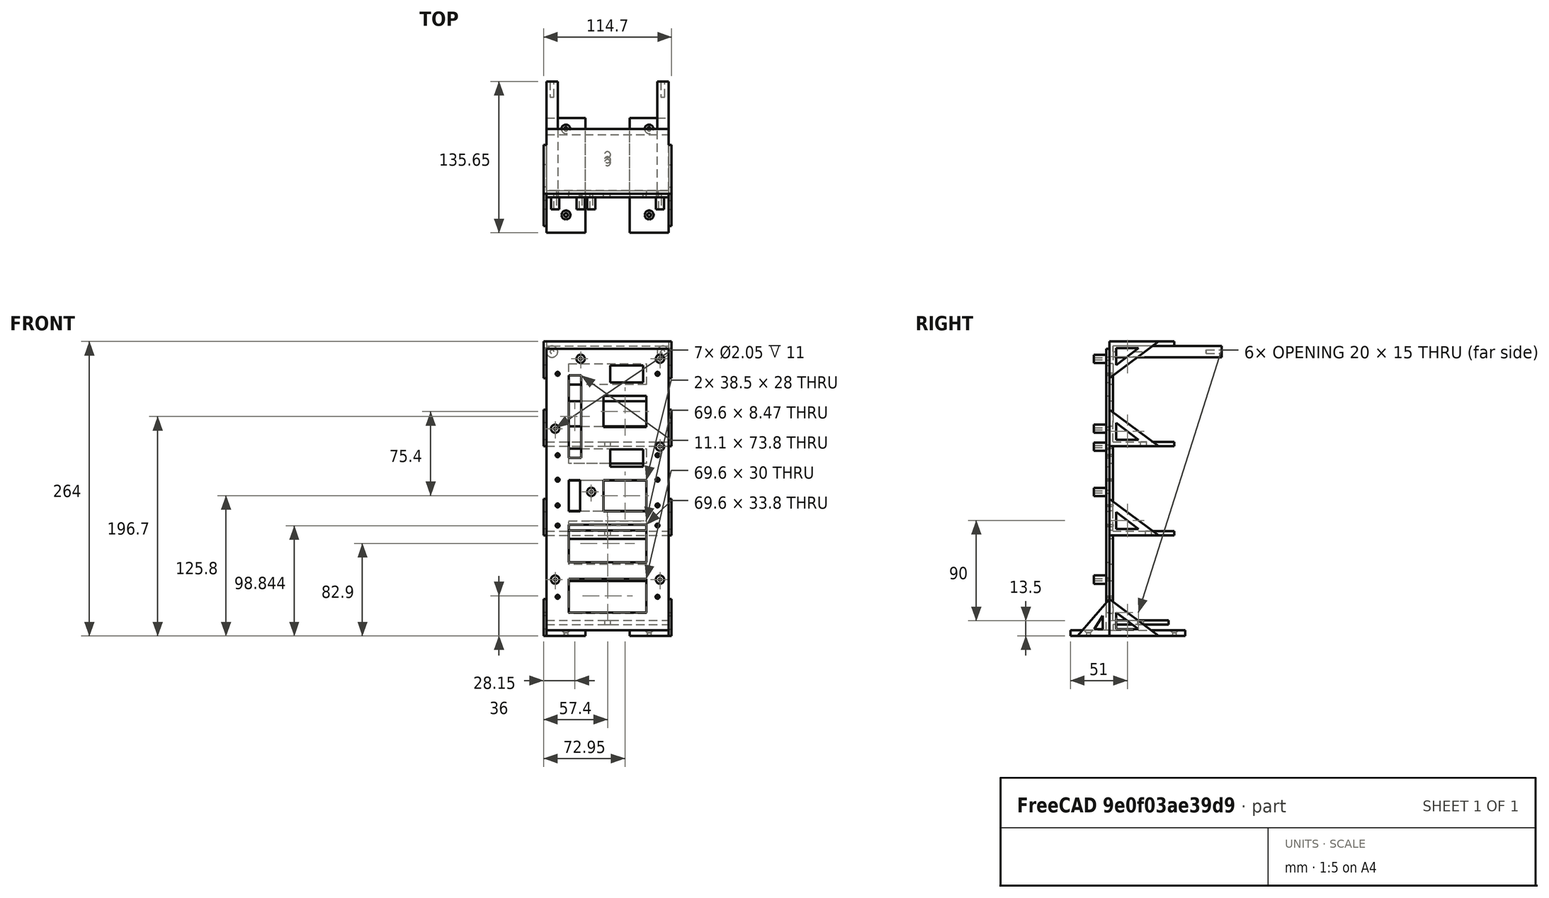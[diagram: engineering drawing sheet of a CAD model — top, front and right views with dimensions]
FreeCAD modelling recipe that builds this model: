
FCSTD DOCUMENT  (FreeCAD 1.0R39109 (Git))
Label: Tower
License: All rights reserved
LicenseURL: http://en.wikipedia.org/wiki/All_rights_reserved
objects: Sketcher::SketchObject×17, PartDesign::Pad×9, PartDesign::Plane×9, PartDesign::Pocket×4, PartDesign::Hole×3, PartDesign::Mirrored×2, PartDesign::Body×2, App::Link×1, App::Part×1
note: 97 computed .brp shape members not serialized (recipe doc carries the construction recipe); baked Part::Feature solids carry a one-line shape summary decoded from their .brp
EXTERNAL_REF file=../Master Document.FCStd obj=Spreadsheet

FEATURE [App::Link] Link  label="Monitor Chassis Parameters"
  LinkedObject = -> <external ../Master Document.FCStd>#Spreadsheet
FEATURE [Sketcher::SketchObject] Sketch  label="Backplate Sketch"
  ArcFitTolerance = 1e-06
  AttachmentSupport = -> [XZ_Plane001]
  FullyConstrained = true
  MakeInternals = false
  MapMode = 5
  Placement = pos=(0,0,0) rot=(1,0,0;1.5708rad)
  expr: Constraints[107] = <<Monitor Chassis Parameters>>.GSBackPlateMinimumSpanWidth
  expr: Constraints[108] = <<Monitor Chassis Parameters>>.GSBackPlateMinimumSpanWidth - 8
  expr: Constraints[109] = <<Monitor Chassis Parameters>>.GSBackPlateMinimumSpanWidth - 5
  expr: Constraints[10] = <<Monitor Chassis Parameters>>.GSComputeBoardWidth / 2 - <<Monitor Chassis Parameters>>.GSBackPlateTopInnerHoleInsetFromSide
  expr: Constraints[118] = 30
  expr: Constraints[119] = <<Monitor Chassis Parameters>>.GSBackPlateMiddleRightHoleHeight
  expr: Constraints[11] = <<Monitor Chassis Parameters>>.GSBackPlateBoltDiameter
  expr: Constraints[120] = <<Monitor Chassis Parameters>>.GSBackPlateTopHolesHeight
  expr: Constraints[122] = <<Monitor Chassis Parameters>>.GSBackPlateMiddleHoleHeight
  expr: Constraints[123] = <<Monitor Chassis Parameters>>.GSBackPlateBottomHoleHeight
  expr: Constraints[126] = <<Monitor Chassis Parameters>>.GSBackPlateLengthIncrement
  expr: Constraints[12] = <<Monitor Chassis Parameters>>.GSComputeBoardWidth / 2 - <<Monitor Chassis Parameters>>.GSBackPlateOuterHolesInsetFromSide
  expr: Constraints[130] = <<Monitor Chassis Parameters>>.GSBackPlateMinimumSpanWidth
  expr: Constraints[131] = <<Monitor Chassis Parameters>>.GSBackPlateMinimumSpanWidth + 4
  expr: Constraints[132] = <<Monitor Chassis Parameters>>.GSBackPlateMinimumSpanWidth
  expr: Constraints[133] = <<Monitor Chassis Parameters>>.GSBackPlateMinimumSpanWidth - 5
  expr: Constraints[134] = <<Monitor Chassis Parameters>>.GSBackPlateWidth
  expr: Constraints[135] = <<Monitor Chassis Parameters>>.GSBackPlateHeight
  expr: Constraints[136] = <<Monitor Chassis Parameters>>.GSBackPlateMiddleLeftHoleHeight
  expr: Constraints[138] = <<Monitor Chassis Parameters>>.GSBackPlateBoltDiameter
  expr: Constraints[13] = <<Monitor Chassis Parameters>>.GSBackPlateBoltDiameter
  expr: Constraints[14] = <<Monitor Chassis Parameters>>.GSComputeBoardWidth / 2 - <<Monitor Chassis Parameters>>.GSBackPlateOuterHolesInsetFromSide
  expr: Constraints[150] = <<Monitor Chassis Parameters>>.GSBackPlateVerticalOffset
  expr: Constraints[15] = <<Monitor Chassis Parameters>>.GSBackPlateBoltDiameter
  expr: Constraints[17] = <<Monitor Chassis Parameters>>.GSComputeBoardWidth / 2 - <<Monitor Chassis Parameters>>.GSBackPlateOuterHolesInsetFromSide
  expr: Constraints[18] = <<Monitor Chassis Parameters>>.GSBackPlateBoltDiameter
  expr: Constraints[19] = <<Monitor Chassis Parameters>>.GSBackPlateWidth / 2 - <<Monitor Chassis Parameters>>.GSBackPlateMiddleHoleOffsetFromLeftSide
  expr: Constraints[20] = <<Monitor Chassis Parameters>>.GSBackPlateBoltDiameter
  expr: Constraints[21] = <<Monitor Chassis Parameters>>.GSBackPlateBoltDiameter
  expr: Constraints[25] = <<Monitor Chassis Parameters>>.GSBackPlateWidthIncrement
  expr: Constraints[73] = <<Monitor Chassis Parameters>>.GSBackPlateMinimumSpanWidth
  expr: Constraints[7] = <<Monitor Chassis Parameters>>.GSComputeBoardHeight
  expr: Constraints[82] = <<Monitor Chassis Parameters>>.GSBackPlateMinimumSpanWidth
  expr: Constraints[8] = <<Monitor Chassis Parameters>>.GSComputeBoardWidth
  expr: Constraints[9] = <<Monitor Chassis Parameters>>.GSComputeBoardWidth / 2
  sketch-geometry (51):
    g0: LineSegment [constr] StartX=-50.8 StartY=20 StartZ=0 EndX=50.8 EndY=20 EndZ=0
    g1: LineSegment [constr] StartX=50.8 StartY=20 StartZ=0 EndX=50.8 EndY=248.6 EndZ=0
    g2: LineSegment [constr] StartX=50.8 StartY=248.6 StartZ=0 EndX=-50.8 EndY=248.6 EndZ=0
    g3: LineSegment [constr] StartX=-50.8 StartY=248.6 StartZ=0 EndX=-50.8 EndY=20 EndZ=0
    g4: Circle CenterX=-24.13 CenterY=243.52 CenterZ=0 NormalX=0 NormalY=0 NormalZ=1 AngleXU=0 Radius=1.4
    g5: Circle CenterX=46.99 CenterY=243.52 CenterZ=0 NormalX=0 NormalY=0 NormalZ=1 AngleXU=0 Radius=1.4
    g6: Circle CenterX=-46.99 CenterY=45.5 CenterZ=0 NormalX=0 NormalY=0 NormalZ=1 AngleXU=0 Radius=1.4
    g7: Circle CenterX=46.99 CenterY=45.5 CenterZ=0 NormalX=0 NormalY=0 NormalZ=1 AngleXU=0 Radius=1.4
    g8: Circle CenterX=-14.668 CenterY=124.14 CenterZ=0 NormalX=0 NormalY=0 NormalZ=1 AngleXU=0 Radius=1.4
    g9: Circle CenterX=-46.99 CenterY=180.78 CenterZ=0 NormalX=0 NormalY=0 NormalZ=1 AngleXU=0 Radius=1.4
    g10: Circle CenterX=46.99 CenterY=164.78 CenterZ=0 NormalX=0 NormalY=0 NormalZ=1 AngleXU=0 Radius=1.4
    g11: LineSegment StartX=-54.8 StartY=252.6 StartZ=0 EndX=-54.8 EndY=16 EndZ=0
    g12: LineSegment [constr] StartX=-54.8 StartY=16 StartZ=0 EndX=54.8 EndY=16 EndZ=0
    g13: LineSegment StartX=31.8 StartY=162.2 StartZ=0 EndX=2.4 EndY=162.2 EndZ=0
    g14: LineSegment StartX=2.4 StartY=162.2 StartZ=0 EndX=2.4 EndY=146.8 EndZ=0
    g15: LineSegment StartX=2.4 StartY=146.8 StartZ=0 EndX=31.8 EndY=146.8 EndZ=0
    g16: LineSegment StartX=31.8 StartY=146.8 StartZ=0 EndX=31.8 EndY=162.2 EndZ=0
    g17: LineSegment StartX=34.8 StartY=106.8 StartZ=0 EndX=-3.7 EndY=106.8 EndZ=0
    g18: LineSegment StartX=-3.7 StartY=106.8 StartZ=0 EndX=-3.7 EndY=134.8 EndZ=0
    g19: LineSegment StartX=-3.7 StartY=134.8 StartZ=0 EndX=34.8 EndY=134.8 EndZ=0
    g20: LineSegment StartX=34.8 StartY=134.8 StartZ=0 EndX=34.8 EndY=106.8 EndZ=0
    g21: LineSegment StartX=31.8 StartY=237.6 StartZ=0 EndX=2.4 EndY=237.6 EndZ=0
    g22: LineSegment StartX=2.4 StartY=237.6 StartZ=0 EndX=2.4 EndY=222.2 EndZ=0
    g23: LineSegment StartX=2.4 StartY=222.2 StartZ=0 EndX=31.8 EndY=222.2 EndZ=0
    g24: LineSegment StartX=31.8 StartY=222.2 StartZ=0 EndX=31.8 EndY=237.6 EndZ=0
    g25: LineSegment StartX=34.8 StartY=182.2 StartZ=0 EndX=-3.7 EndY=182.2 EndZ=0
    g26: LineSegment StartX=-3.7 StartY=182.2 StartZ=0 EndX=-3.7 EndY=210.2 EndZ=0
    g27: LineSegment StartX=-3.7 StartY=210.2 StartZ=0 EndX=34.8 EndY=210.2 EndZ=0
    g28: LineSegment StartX=34.8 StartY=210.2 StartZ=0 EndX=34.8 EndY=182.2 EndZ=0
    g29: LineSegment StartX=-34.8 StartY=228.6 StartZ=0 EndX=-34.8 EndY=154.8 EndZ=0
    g30: LineSegment StartX=-34.8 StartY=154.8 StartZ=0 EndX=-23.7 EndY=154.8 EndZ=0
    g31: LineSegment StartX=-23.7 StartY=154.8 StartZ=0 EndX=-23.7 EndY=228.6 EndZ=0
    g32: LineSegment StartX=-23.7 StartY=228.6 StartZ=0 EndX=-34.8 EndY=228.6 EndZ=0
    g33: LineSegment StartX=-34.8 StartY=134.8 StartZ=0 EndX=-34.8 EndY=106.8 EndZ=0
    g34: LineSegment StartX=-34.8 StartY=106.8 StartZ=0 EndX=-24.668 EndY=106.8 EndZ=0
    g35: LineSegment StartX=-24.668 StartY=106.8 StartZ=0 EndX=-24.668 EndY=134.8 EndZ=0
    g36: LineSegment StartX=-24.668 StartY=134.8 StartZ=0 EndX=-34.8 EndY=134.8 EndZ=0
    g37: LineSegment StartX=-34.8 StartY=94.8 StartZ=0 EndX=-34.8 EndY=61 EndZ=0
    g38: LineSegment StartX=-34.8 StartY=61 StartZ=0 EndX=34.8 EndY=61 EndZ=0
    g39: LineSegment StartX=34.8 StartY=61 StartZ=0 EndX=34.8 EndY=94.8 EndZ=0
    g40: LineSegment StartX=34.8 StartY=94.8 StartZ=0 EndX=-34.8 EndY=94.8 EndZ=0
    g41: LineSegment StartX=-34.8 StartY=46 StartZ=0 EndX=-34.8 EndY=16 EndZ=0
    g42: LineSegment StartX=-34.8 StartY=16 StartZ=0 EndX=34.8 EndY=16 EndZ=0
    g43: LineSegment StartX=34.8 StartY=16 StartZ=0 EndX=34.8 EndY=46 EndZ=0
    g44: LineSegment StartX=34.8 StartY=46 StartZ=0 EndX=-34.8 EndY=46 EndZ=0
    g45: LineSegment StartX=54.8 StartY=16 StartZ=0 EndX=54.8 EndY=252.6 EndZ=0
    g46: LineSegment StartX=-54.8 StartY=252.6 StartZ=0 EndX=54.8 EndY=252.6 EndZ=0
    g47: LineSegment StartX=-54.8 StartY=16 StartZ=0 EndX=-54.8 EndY=0 EndZ=0
    g48: LineSegment StartX=-54.8 StartY=0 StartZ=0 EndX=54.8 EndY=0 EndZ=0
    g49: LineSegment StartX=54.8 StartY=0 StartZ=0 EndX=54.8 EndY=16 EndZ=0
    g50: LineSegment [constr] StartX=54.8 StartY=16 StartZ=0 EndX=-54.8 EndY=16 EndZ=0
  constraints (152):
    c: Coincident(g0,g1)
    c: Coincident(g1,g2)
    c: Coincident(g2,g3)
    c: Coincident(g3,g0)
    c: Horizontal(g2)
    c: Vertical(g1)
    c: Vertical(g3)
    c: DistanceY(g0,g2) = 228.6
    c: DistanceX(g0,g0) = 101.6
    c: DistanceX(g0,g-1) = 50.8
    c: DistanceX(g4,g-1) = 24.13
    c: Diameter(g4) = 2.8
    c: DistanceX(g-1,g5) = 46.99
    c: Diameter(g6) = 2.8
    c: DistanceX(g6,g-1) = 46.99
    c: Diameter(g7) = 2.8
    c: Horizontal(g7,g6)
    c: DistanceX(g-1,g7) = 46.99
    c: Diameter(g8) = 2.8
    c: DistanceX(g8,g-1) = 14.668
    c: Diameter(g9) = 2.8
    c: Diameter(g10) = 2.8
    c: Coincident(g11,g12)
    c: Vertical(g11)
    c: Horizontal(g12)
    c: DistanceX(g11,g0) = 4
    c: Horizontal(g0)
    c: Vertical(g6,g9)
    c: Coincident(g13,g14)
    c: Coincident(g14,g15)
    c: Coincident(g15,g16)
    c: Coincident(g16,g13)
    c: Horizontal(g13)
    c: Horizontal(g15)
    c: Vertical(g14)
    c: Vertical(g16)
    c: Coincident(g17,g18)
    c: Coincident(g18,g19)
    c: Coincident(g19,g20)
    c: Coincident(g20,g17)
    c: Horizontal(g17)
    c: Horizontal(g19)
    c: Vertical(g18)
    c: Vertical(g20)
    c: DistanceX(g13,g13) = 29.4
    c: DistanceY(g14,g13) = 15.4
    c: DistanceX(g18,g19) = 38.5
    c: DistanceY(g17,g18) = 28
    c: DistanceY(g19,g15) = 12
    c: DistanceX(g15,g19) = 3
    c: Coincident(g21,g22)
    c: Coincident(g22,g23)
    c: Coincident(g23,g24)
    c: Coincident(g24,g21)
    c: Horizontal(g21)
    c: Horizontal(g23)
    c: Vertical(g22)
    c: Vertical(g24)
    c: Coincident(g25,g26)
    c: Coincident(g26,g27)
    c: Coincident(g27,g28)
    c: Coincident(g28,g25)
    c: Horizontal(g25)
    c: Horizontal(g27)
    c: Vertical(g26)
    c: Vertical(g28)
    c: DistanceX(g21,g21) = 29.4
    c: DistanceY(g22,g21) = 15.4
    c: DistanceX(g26,g27) = 38.5
    c: DistanceY(g25,g26) = 28
    c: DistanceY(g27,g23) = 12
    c: DistanceX(g23,g27) = 3
    c: Vertical(g19,g25)
    c: DistanceY(g13,g25) = 20
    c: Coincident(g29,g30)
    c: Coincident(g30,g31)
    c: Coincident(g31,g32)
    c: Coincident(g32,g29)
    c: Vertical(g29)
    c: Vertical(g31)
    c: Horizontal(g30)
    c: Horizontal(g32)
    c: DistanceX(g31,g26) = 20
    c: Coincident(g33,g34)
    c: Coincident(g34,g35)
    c: Coincident(g35,g36)
    c: Coincident(g36,g33)
    c: Vertical(g33)
    c: Vertical(g35)
    c: Horizontal(g34)
    c: Horizontal(g36)
    c: Coincident(g37,g38)
    c: Coincident(g38,g39)
    c: Coincident(g39,g40)
    c: Coincident(g40,g37)
    c: Vertical(g37)
    c: Vertical(g39)
    c: Horizontal(g38)
    c: Horizontal(g40)
    c: Coincident(g41,g42)
    c: Coincident(g42,g43)
    c: Coincident(g43,g44)
    c: Coincident(g44,g41)
    c: Vertical(g41)
    c: Vertical(g43)
    c: Horizontal(g42)
    c: Horizontal(g44)
    c: DistanceY(g33,g29) = 20
    c: DistanceY(g37,g33) = 12
    c: DistanceY(g41,g37) = 15
    c: Vertical(g29,g33)
    c: Vertical(g33,g37)
    c: Vertical(g37,g41)
    c: Vertical(g17,g39)
    c: Vertical(g39,g43)
    c: Horizontal(g35,g18)
    c: DistanceX(g35,g8) = 10
    c: Horizontal(g34,g17)
    c: DistanceY(g41,g41) = 30
    c: DistanceY(g0,g10) = 144.78
    c: DistanceY(g0,g4) = 223.52
    c: Horizontal(g5,g4)
    c: DistanceY(g0,g8) = 104.14
    c: DistanceY(g0,g6) = 25.5
    c: Coincident(g45,g12)
    c: Vertical(g45)
    c: DistanceY(g1,g45) = 4
    c: Horizontal(g11,g45)
    c: Coincident(g46,g11)
    c: Coincident(g46,g45)
    c: DistanceX(g11,g29) = 20
    c: DistanceY(g29,g11) = 24
    c: DistanceX(g27,g45) = 20
    c: DistanceY(g21,g45) = 15
    c: DistanceX(g11,g12) = 109.6
    c: DistanceY(g11,g11) = 236.6
    c: DistanceY(g0,g9) = 160.78
    c: Vertical(g7,g10)
    c: Diameter(g5) = 2.8
    c: Coincident(g47,g48)
    c: Coincident(g48,g49)
    c: Coincident(g49,g50)
    c: Coincident(g50,g47)
    c: Vertical(g47)
    c: Vertical(g49)
    c: Horizontal(g48)
    c: Horizontal(g50)
    c: Coincident(g47,g11)
    c: Horizontal(g48,g-1)
    c: Vertical(g49,g12)
    c: DistanceY(g-1,g0) = 20
    c: Horizontal(g41,g11)
FEATURE [PartDesign::Pad] Pad  label="Backplate Pad"
  Direction = (0,-1,2e-16)
  Length = 3
  Length2 = 10
  Placement = pos=(0,0,0) rot=(1,0,0;1.5708rad)
  Profile = -> Sketch
  ReferenceAxis = -> Sketch [N_Axis]
  Reversed = true
  Suppressed = false
  Type = 0
  expr: Length = <<Monitor Chassis Parameters>>.GSBackPlateThickness
FEATURE [Sketcher::SketchObject] Sketch001  label="Backplate Risers Sketch"
  ArcFitTolerance = 1e-06
  AttachmentSupport = -> [XZ_Plane001]
  FullyConstrained = true
  MakeInternals = false
  MapMode = 5
  Placement = pos=(0,0,0) rot=(1,0,0;1.5708rad)
  expr: Constraints[10] = <<Monitor Chassis Parameters>>.GSM2_5TappingScrewHoleDiameter
  expr: Constraints[11] = <<Monitor Chassis Parameters>>.GSM2_5TappingScrewHoleDiameter
  expr: Constraints[12] = <<Monitor Chassis Parameters>>.GSComputeBoardWidth / 2 - <<Monitor Chassis Parameters>>.GSBackPlateOuterHolesInsetFromSide
  expr: Constraints[13] = <<Monitor Chassis Parameters>>.GSM2_5TappingScrewHoleDiameter
  expr: Constraints[14] = <<Monitor Chassis Parameters>>.GSComputeBoardWidth / 2 - <<Monitor Chassis Parameters>>.GSBackPlateOuterHolesInsetFromSide
  expr: Constraints[15] = <<Monitor Chassis Parameters>>.GSM2_5TappingScrewHoleDiameter
  expr: Constraints[16] = <<Monitor Chassis Parameters>>.GSComputeBoardWidth / 2 - <<Monitor Chassis Parameters>>.GSBackPlateOuterHolesInsetFromSide
  expr: Constraints[17] = <<Monitor Chassis Parameters>>.GSM2_5TappingScrewHoleDiameter
  expr: Constraints[18] = <<Monitor Chassis Parameters>>.GSBackPlateWidth / 2 - <<Monitor Chassis Parameters>>.GSBackPlateMiddleHoleOffsetFromLeftSide
  expr: Constraints[19] = <<Monitor Chassis Parameters>>.GSM2_5TappingScrewHoleDiameter
  expr: Constraints[20] = <<Monitor Chassis Parameters>>.GSM2_5TappingScrewHoleDiameter
  expr: Constraints[25] = <<Monitor Chassis Parameters>>.GSBackPlateScrewHoleDiameter + 2 * <<Monitor Chassis Parameters>>.GSBackPlateStandoffWallThickness
  expr: Constraints[27] = <<Monitor Chassis Parameters>>.GSBackPlateScrewHoleDiameter + 2 * <<Monitor Chassis Parameters>>.GSBackPlateStandoffWallThickness
  expr: Constraints[33] = <<Monitor Chassis Parameters>>.GSBackPlateScrewHoleDiameter + 2 * <<Monitor Chassis Parameters>>.GSBackPlateStandoffWallThickness
  expr: Constraints[34] = <<Monitor Chassis Parameters>>.GSBackPlateScrewHoleDiameter + 2 * <<Monitor Chassis Parameters>>.GSBackPlateStandoffWallThickness
  expr: Constraints[35] = <<Monitor Chassis Parameters>>.GSBackPlateScrewHoleDiameter + 2 * <<Monitor Chassis Parameters>>.GSBackPlateStandoffWallThickness
  expr: Constraints[36] = <<Monitor Chassis Parameters>>.GSBackPlateScrewHoleDiameter + 2 * <<Monitor Chassis Parameters>>.GSBackPlateStandoffWallThickness
  expr: Constraints[37] = <<Monitor Chassis Parameters>>.GSBackPlateScrewHoleDiameter + 2 * <<Monitor Chassis Parameters>>.GSBackPlateStandoffWallThickness
  expr: Constraints[39] = <<Monitor Chassis Parameters>>.GSBackPlateMiddleLeftHoleHeight
  expr: Constraints[40] = <<Monitor Chassis Parameters>>.GSBackPlateBottomHoleHeight
  expr: Constraints[42] = <<Monitor Chassis Parameters>>.GSBackPlateMiddleHoleHeight
  expr: Constraints[43] = <<Monitor Chassis Parameters>>.GSBackPlateTopHolesHeight
  expr: Constraints[44] = <<Monitor Chassis Parameters>>.GSBackPlateMiddleRightHoleHeight
  expr: Constraints[45] = <<Monitor Chassis Parameters>>.GSBackPlateVerticalOffset
  expr: Constraints[6] = <<Monitor Chassis Parameters>>.GSComputeBoardHeight
  expr: Constraints[7] = <<Monitor Chassis Parameters>>.GSComputeBoardWidth
  expr: Constraints[8] = <<Monitor Chassis Parameters>>.GSComputeBoardWidth / 2
  expr: Constraints[9] = 0.5 * <<Monitor Chassis Parameters>>.GSComputeBoardWidth - <<Monitor Chassis Parameters>>.GSBackPlateTopInnerHoleInsetFromSide
  sketch-geometry (18):
    g0: LineSegment [constr] StartX=-50.8 StartY=20 StartZ=0 EndX=50.8 EndY=20 EndZ=0
    g1: LineSegment [constr] StartX=50.8 StartY=20 StartZ=0 EndX=50.8 EndY=248.6 EndZ=0
    g2: LineSegment [constr] StartX=50.8 StartY=248.6 StartZ=0 EndX=-50.8 EndY=248.6 EndZ=0
    g3: LineSegment [constr] StartX=-50.8 StartY=248.6 StartZ=0 EndX=-50.8 EndY=20 EndZ=0
    g4: Circle CenterX=-24.13 CenterY=243.52 CenterZ=0 NormalX=0 NormalY=0 NormalZ=1 AngleXU=0 Radius=1.025
    g5: Circle CenterX=46.99 CenterY=243.52 CenterZ=0 NormalX=0 NormalY=0 NormalZ=1 AngleXU=0 Radius=1.025
    g6: Circle CenterX=-46.99 CenterY=45.5 CenterZ=0 NormalX=0 NormalY=0 NormalZ=1 AngleXU=0 Radius=1.025
    g7: Circle CenterX=46.99 CenterY=45.5 CenterZ=0 NormalX=0 NormalY=0 NormalZ=1 AngleXU=0 Radius=1.025
    g8: Circle CenterX=-14.668 CenterY=124.14 CenterZ=0 NormalX=0 NormalY=0 NormalZ=1 AngleXU=0 Radius=1.025
    g9: Circle CenterX=-46.99 CenterY=180.78 CenterZ=0 NormalX=0 NormalY=0 NormalZ=1 AngleXU=0 Radius=1.025
    g10: Circle CenterX=46.99 CenterY=164.78 CenterZ=0 NormalX=0 NormalY=0 NormalZ=1 AngleXU=0 Radius=1.025
    g11: Circle CenterX=-24.13 CenterY=243.52 CenterZ=0 NormalX=0 NormalY=0 NormalZ=1 AngleXU=0 Radius=3.7
    g12: Circle CenterX=46.99 CenterY=243.52 CenterZ=0 NormalX=0 NormalY=0 NormalZ=1 AngleXU=0 Radius=3.7
    g13: Circle CenterX=-46.99 CenterY=180.78 CenterZ=0 NormalX=0 NormalY=0 NormalZ=1 AngleXU=0 Radius=3.7
    g14: Circle CenterX=46.99 CenterY=164.78 CenterZ=0 NormalX=0 NormalY=0 NormalZ=1 AngleXU=0 Radius=3.7
    g15: Circle CenterX=-14.668 CenterY=124.14 CenterZ=0 NormalX=0 NormalY=0 NormalZ=1 AngleXU=0 Radius=3.7
    g16: Circle CenterX=-46.99 CenterY=45.5 CenterZ=0 NormalX=0 NormalY=0 NormalZ=1 AngleXU=0 Radius=3.7
    g17: Circle CenterX=46.99 CenterY=45.5 CenterZ=0 NormalX=0 NormalY=0 NormalZ=1 AngleXU=0 Radius=3.7
  constraints (47):
    c: Coincident(g0,g1)
    c: Coincident(g1,g2)
    c: Coincident(g2,g3)
    c: Coincident(g3,g0)
    c: Vertical(g1)
    c: Vertical(g3)
    c: DistanceY(g0,g2) = 228.6
    c: DistanceX(g0,g0) = 101.6
    c: DistanceX(g0,g-1) = 50.8
    c: DistanceX(g4,g-1) = 24.13
    c: Diameter(g4) = 2.05
    c: Diameter(g5) = 2.05
    c: DistanceX(g-1,g5) = 46.99
    c: Diameter(g6) = 2.05
    c: DistanceX(g6,g-1) = 46.99
    c: Diameter(g7) = 2.05
    c: DistanceX(g-1,g7) = 46.99
    c: Diameter(g8) = 2.05
    c: DistanceX(g8,g-1) = 14.668
    c: Diameter(g9) = 2.05
    c: Diameter(g10) = 2.05
    c: Horizontal(g0)
    c: Vertical(g5,g10)
    c: Horizontal(g5,g4)
    c: Coincident(g11,g4)
    c: Diameter(g11) = 7.4
    c: Coincident(g12,g5)
    c: Diameter(g12) = 7.4
    c: Coincident(g13,g9)
    c: Coincident(g14,g10)
    c: Coincident(g15,g8)
    c: Coincident(g16,g6)
    c: Coincident(g17,g7)
    c: Diameter(g17) = 7.4
    c: Diameter(g16) = 7.4
    c: Diameter(g15) = 7.4
    c: Diameter(g14) = 7.4
    c: Diameter(g13) = 7.4
    c: Vertical(g9,g6)
    c: DistanceY(g0,g9) = 160.78
    c: DistanceY(g0,g6) = 25.5
    c: Horizontal(g7,g6)
    c: DistanceY(g0,g8) = 104.14
    c: DistanceY(g0,g4) = 223.52
    c: DistanceY(g0,g10) = 144.78
    c: DistanceY(g-1,g0) = 20
    c: Horizontal(g2,g1)
FEATURE [PartDesign::Pad] Pad001  label="Backplate Risers Pad"
  BaseFeature = -> Pad
  Direction = (0,-1,2e-16)
  Length = 11
  Length2 = 10
  Placement = pos=(0,0,0) rot=(1,0,0;1.5708rad)
  Profile = -> Sketch001
  ReferenceAxis = -> Sketch001 [N_Axis]
  Suppressed = false
  Type = 0
  expr: Length = <<Monitor Chassis Parameters>>.GSBackPlateStandoffHeight
FEATURE [Sketcher::SketchObject] Sketch002  label="Backplate Foot Sketch"
  ArcFitTolerance = 1e-06
  AttachmentSupport = -> [XZ_Plane001]
  FullyConstrained = true
  MakeInternals = false
  MapMode = 5
  Placement = pos=(0,0,0) rot=(1,0,0;1.5708rad)
  expr: Constraints[11] = <<Monitor Chassis Parameters>>.GSTowerFeetThickness
  expr: Constraints[21] = <<Monitor Chassis Parameters>>.GSTowerFeetThickness
  expr: Constraints[22] = <<Monitor Chassis Parameters>>.GSBackPlateFootWidth
  expr: Constraints[23] = 0.5 * <<Monitor Chassis Parameters>>.GSBackPlateWidth
  expr: Constraints[8] = <<Monitor Chassis Parameters>>.GSBackPlateFootWidth
  expr: Constraints[9] = 0.5 * <<Monitor Chassis Parameters>>.GSBackPlateWidth
  sketch-geometry (8):
    g0: LineSegment StartX=-54.8 StartY=-5 StartZ=0 EndX=-19.8 EndY=-5 EndZ=0
    g1: LineSegment StartX=-19.8 StartY=-5 StartZ=0 EndX=-19.8 EndY=0 EndZ=0
    g2: LineSegment StartX=-19.8 StartY=0 StartZ=0 EndX=-54.8 EndY=0 EndZ=0
    g3: LineSegment StartX=-54.8 StartY=0 StartZ=0 EndX=-54.8 EndY=-5 EndZ=0
    g4: LineSegment StartX=54.8 StartY=-5 StartZ=0 EndX=54.8 EndY=0 EndZ=0
    g5: LineSegment StartX=54.8 StartY=0 StartZ=0 EndX=19.8 EndY=0 EndZ=0
    g6: LineSegment StartX=19.8 StartY=0 StartZ=0 EndX=19.8 EndY=-5 EndZ=0
    g7: LineSegment StartX=19.8 StartY=-5 StartZ=0 EndX=54.8 EndY=-5 EndZ=0
  constraints (24):
    c: Coincident(g0,g1)
    c: Coincident(g1,g2)
    c: Coincident(g2,g3)
    c: Coincident(g3,g0)
    c: Horizontal(g0)
    c: Horizontal(g2)
    c: Vertical(g1)
    c: Vertical(g3)
    c: DistanceX(g2,g1) = 35
    c: DistanceX(g2,g-1) = 54.8
    c: Horizontal(g2,g-1)
    c: DistanceY(g0,g2) = 5
    c: Coincident(g4,g5)
    c: Coincident(g5,g6)
    c: Coincident(g6,g7)
    c: Coincident(g7,g4)
    c: Vertical(g4)
    c: Vertical(g6)
    c: Horizontal(g5)
    c: Horizontal(g7)
    c: Horizontal(g5,g-1)
    c: DistanceY(g4,g4) = 5
    c: DistanceX(g6,g4) = 35
    c: DistanceX(g-1,g4) = 54.8
FEATURE [PartDesign::Pad] Pad002  label="Backplate Foot Pad"
  BaseFeature = -> Pad001
  Direction = (0,-1,2e-16)
  Length = 32
  Length2 = 3
  Placement = pos=(0,0,0) rot=(1,0,0;1.5708rad)
  Profile = -> Sketch002
  ReferenceAxis = -> Sketch002 [N_Axis]
  Suppressed = false
  Type = 4
  expr: Length = <<Monitor Chassis Parameters>>.GSBackPlateFootLengthBackward
  expr: Length2 = <<Monitor Chassis Parameters>>.GSBackPlateThickness
FEATURE [Sketcher::SketchObject] Sketch003  label="Backplate Foot Screw Holes Sketch"
  ArcFitTolerance = 1e-06
  AttachmentSupport = -> [XY_Plane001]
  FullyConstrained = true
  MakeInternals = false
  MapMode = 5
  expr: Constraints[0] = 0.5 * <<Monitor Chassis Parameters>>.GSBackPlateFootLengthBackward
  expr: Constraints[1] = 0.5 * <<Monitor Chassis Parameters>>.GSBackPlateWidth - 0.5 * <<Monitor Chassis Parameters>>.GSBackPlateFootWidth
  expr: Constraints[2] = 0.5 * <<Monitor Chassis Parameters>>.GSBackPlateWidth - 0.5 * <<Monitor Chassis Parameters>>.GSBackPlateFootWidth
  expr: Constraints[3] = <<Monitor Chassis Parameters>>.GSTowerFeetScrewDiameter
  expr: Constraints[4] = <<Monitor Chassis Parameters>>.GSTowerFeetScrewDiameter
  sketch-geometry (2):
    g0: Circle CenterX=-37.3 CenterY=-16 CenterZ=0 NormalX=0 NormalY=0 NormalZ=1 AngleXU=0 Radius=1.7
    g1: Circle CenterX=37.3 CenterY=-16 CenterZ=0 NormalX=0 NormalY=0 NormalZ=1 AngleXU=0 Radius=1.7
  constraints (6):
    c: DistanceY(g0,g-1) = 16
    c: DistanceX(g0,g-1) = 37.3
    c: DistanceX(g-1,g1) = 37.3
    c: Diameter(g0) = 3.4
    c: Diameter(g1) = 3.4
    c: Horizontal(g1,g0)
FEATURE [PartDesign::Hole] Hole  label="Backplate Foot Screw Holes"
  BaseFeature = -> Pad002
  CustomThreadClearance = 0
  Depth = 25
  DepthType = 0
  Diameter = 3.4
  DrillForDepth = false
  DrillPoint = 1
  DrillPointAngle = 118
  HoleCutCountersinkAngle = 90
  HoleCutCustomValues = false
  HoleCutDepth = 0
  HoleCutDiameter = 8
  HoleCutType = 2
  ModelThread = false
  Placement = pos=(0,0,0) rot=(1,0,0;1.5708rad)
  Profile = -> Sketch003
  Suppressed = false
  Tapered = false
  TaperedAngle = 90
  ThreadClass = 0
  ThreadDepth = 25
  ThreadDepthType = 0
  ThreadDirection = 0
  ThreadFit = 0
  ThreadSize = 0
  ThreadType = 0
  Threaded = false
  UseCustomThreadClearance = false
  expr: Diameter = <<Monitor Chassis Parameters>>.GSTowerFeetScrewDiameter
  expr: HoleCutDiameter = <<Monitor Chassis Parameters>>.GSM4BoltCountersinkDiameter
FEATURE [PartDesign::Plane] DatumPlane
  AttachmentOffset = pos=(0,0,54.8) rot=(0,0,1;0rad)
  AttachmentSupport = -> [YZ_Plane001]
  Length = 82.1581
  MapMode = 5
  Placement = pos=(54.8,0,0) rot=(0.57735,0.57735,0.57735;2.0944rad)
  ResizeMode = 0
  Width = 302.758
  expr: .AttachmentOffset.Base.z = 0.5 * <<Monitor Chassis Parameters>>.GSBackPlateWidth
FEATURE [Sketcher::SketchObject] Sketch004  label="Foot Support Corner Sketch"
  ArcFitTolerance = 1e-06
  AttachmentSupport = -> [DatumPlane]
  FullyConstrained = true
  MakeInternals = false
  MapMode = 5
  Placement = pos=(54.8,0,0) rot=(0.57735,0.57735,0.57735;2.0944rad)
  expr: Constraints[14] = <<Monitor Chassis Parameters>>.GSSideCornerCutoutInset
  expr: Constraints[15] = <<Monitor Chassis Parameters>>.GSSideCornerCutoutInset
  expr: Constraints[16] = 2.5 * <<Monitor Chassis Parameters>>.GSSideCornerCutoutInset
  expr: Constraints[17] = 2.5 * <<Monitor Chassis Parameters>>.GSSideCornerCutoutInset
  expr: Constraints[1] = <<Monitor Chassis Parameters>>.GSBackPlateThickness
  expr: Constraints[4] = <<Monitor Chassis Parameters>>.GSTowerFeetThickness
  expr: Constraints[7] = 0.9 * <<Monitor Chassis Parameters>>.GSBackPlateFootLengthBackward
  expr: Constraints[8] = 0.6 * <<Monitor Chassis Parameters>>.GSTowerFloorDepth
  sketch-geometry (6):
    g0: LineSegment StartX=-25.8 StartY=-5 StartZ=0 EndX=3 EndY=-5 EndZ=0
    g1: LineSegment StartX=3 StartY=28 StartZ=0 EndX=3 EndY=-5 EndZ=0
    g2: LineSegment StartX=-25.8 StartY=-5 StartZ=0 EndX=3 EndY=28 EndZ=0
    g3: LineSegment StartX=-10.8 StartY=1 StartZ=0 EndX=-3 EndY=13 EndZ=0
    g4: LineSegment StartX=-3 StartY=13 StartZ=0 EndX=-3 EndY=1 EndZ=0
    g5: LineSegment StartX=-10.8 StartY=1 StartZ=0 EndX=-3 EndY=1 EndZ=0
  constraints (18):
    c: Horizontal(g0)
    c: DistanceX(g-1,g0) = 3
    c: Coincident(g1,g0)
    c: Vertical(g1)
    c: DistanceY(g0,g-1) = 5
    c: Coincident(g2,g0)
    c: Coincident(g2,g1)
    c: DistanceX(g0,g0) = 28.8
    c: DistanceY(g0,g1) = 33
    c: Coincident(g4,g3)
    c: Vertical(g4)
    c: Coincident(g5,g3)
    c: Coincident(g5,g4)
    c: Horizontal(g5)
    c: DistanceY(g0,g4) = 6
    c: DistanceX(g4,g0) = 6
    c: DistanceX(g0,g3) = 15
    c: DistanceY(g3,g1) = 15
FEATURE [PartDesign::Pad] Pad003  label="Foot Support Corner Pad"
  BaseFeature = -> Hole
  Direction = (1,0,0)
  Length = 2.5
  Length2 = 10
  Placement = pos=(0,0,0) rot=(1,0,0;1.5708rad)
  Profile = -> Sketch004
  ReferenceAxis = -> Sketch004 [N_Axis]
  Suppressed = false
  Type = 0
  expr: Length = <<Monitor Chassis Parameters>>.GSSideCornerThickness
FEATURE [PartDesign::Mirrored] Mirrored  label="Foot Support Corner Mirrored"
  BaseFeature = -> Pad003
  MirrorPlane = -> YZ_Plane001
  Originals = -> [Pad003]
  Placement = pos=(0,0,0) rot=(1,0,0;1.5708rad)
  Suppressed = false
  TransformMode = 0
FEATURE [PartDesign::Plane] DatumPlane001
  AttachmentOffset = pos=(0,0,54.8) rot=(0,0,1;0rad)
  AttachmentSupport = -> [YZ_Plane002]
  Length = 159.977
  MapMode = 5
  Placement = pos=(54.8,0,0) rot=(0.57735,0.57735,0.57735;2.0944rad)
  ResizeMode = 0
  Width = 321.327
  expr: .AttachmentOffset.Base.z = 0.5 * <<Monitor Chassis Parameters>>.GSBackPlateWidth
FEATURE [Sketcher::SketchObject] Sketch005  label="Frontplate Sketch"
  ArcFitTolerance = 1e-06
  AttachmentSupport = -> [XZ_Plane002]
  FullyConstrained = false
  MakeInternals = false
  MapMode = 5
  Placement = pos=(0,0,0) rot=(1,0,0;1.5708rad)
  expr: Constraints[105] = <<Monitor Chassis Parameters>>.GSFrontPlateMinimumSpanWidth - 5
  expr: Constraints[106] = <<Monitor Chassis Parameters>>.GSTowerFourthFloorHeight + <<Monitor Chassis Parameters>>.GSTowerFloorThickness
  expr: Constraints[107] = <<Monitor Chassis Parameters>>.GSTowerLayerJoinScrewDiameter
  expr: Constraints[108] = <<Monitor Chassis Parameters>>.GSTowerLayerJoinScrewDiameter
  expr: Constraints[110] = <<Monitor Chassis Parameters>>.GSTowerLayerJoinScrewInset
  expr: Constraints[111] = <<Monitor Chassis Parameters>>.GSTowerLayerJoinScrewInset
  expr: Constraints[112] = <<Monitor Chassis Parameters>>.GSTowerLayerJoinScrewDiameter
  expr: Constraints[113] = <<Monitor Chassis Parameters>>.GSTowerLayerJoinScrewDiameter
  expr: Constraints[115] = <<Monitor Chassis Parameters>>.GSTowerLayerJoinScrewDiameter
  expr: Constraints[116] = <<Monitor Chassis Parameters>>.GSTowerLayerJoinScrewDiameter
  expr: Constraints[120] = <<Monitor Chassis Parameters>>.GSTowerLayerJoinScrewDiameter
  expr: Constraints[121] = <<Monitor Chassis Parameters>>.GSTowerLayerJoinScrewDiameter
  expr: Constraints[123] = <<Monitor Chassis Parameters>>.GSTowerLayerJoinScrewHeightFromFoot_1
  expr: Constraints[124] = <<Monitor Chassis Parameters>>.GSTowerLayerJoinScrewHeightFromFoot_3
  expr: Constraints[126] = <<Monitor Chassis Parameters>>.GSTowerLayerJoinScrewHeightFromFoot_4
  expr: Constraints[127] = <<Monitor Chassis Parameters>>.GSTowerLayerJoinScrewHeightFromFoot_5
  expr: Constraints[129] = <<Monitor Chassis Parameters>>.GSTowerLayerJoinScrewDiameter
  expr: Constraints[130] = <<Monitor Chassis Parameters>>.GSTowerLayerJoinScrewDiameter
  expr: Constraints[133] = <<Monitor Chassis Parameters>>.GSTowerLayerJoinScrewHeightFromFoot_6
  expr: Constraints[13] = <<Monitor Chassis Parameters>>.GSBackPlateWidthIncrement
  expr: Constraints[145] = <<Monitor Chassis Parameters>>.GSTowerLayerJoinScrewDiameter
  expr: Constraints[150] = <<Monitor Chassis Parameters>>.GSTowerLayerJoinScrewHeightFromFoot_2
  expr: Constraints[46] = <<Monitor Chassis Parameters>>.GSFrontPlateMinimumSpanWidth - 5
  expr: Constraints[48] = <<Monitor Chassis Parameters>>.GSFrontPlateMinimumSpanWidth
  expr: Constraints[65] = <<Monitor Chassis Parameters>>.GSFrontPlateMinimumSpanWidth - 5
  expr: Constraints[71] = <<Monitor Chassis Parameters>>.GSBackPlateLengthIncrement
  expr: Constraints[75] = <<Monitor Chassis Parameters>>.GSBackPlateWidth
  expr: Constraints[76] = <<Monitor Chassis Parameters>>.GSBackPlateVerticalOffset
  expr: Constraints[7] = <<Monitor Chassis Parameters>>.GSComputeBoardHeight
  expr: Constraints[8] = <<Monitor Chassis Parameters>>.GSComputeBoardWidth
  expr: Constraints[96] = <<Monitor Chassis Parameters>>.GSFrontPlateMinimumSpanWidth - 5
  expr: Constraints[97] = <<Monitor Chassis Parameters>>.GSFrontPlateMinimumSpanWidth
  expr: Constraints[98] = <<Monitor Chassis Parameters>>.GSFrontPlateMinimumSpanWidth
  expr: Constraints[9] = <<Monitor Chassis Parameters>>.GSComputeBoardWidth / 2
  sketch-geometry (55):
    g0: LineSegment [constr] StartX=-50.8 StartY=24 StartZ=0 EndX=50.8 EndY=24 EndZ=0
    g1: LineSegment [constr] StartX=50.8 StartY=24 StartZ=0 EndX=50.8 EndY=252.6 EndZ=0
    g2: LineSegment [constr] StartX=50.8 StartY=252.6 StartZ=0 EndX=-50.8 EndY=252.6 EndZ=0
    g3: LineSegment [constr] StartX=-50.8 StartY=252.6 StartZ=0 EndX=-50.8 EndY=24 EndZ=0
    g4: LineSegment StartX=-54.8 StartY=256.6 StartZ=0 EndX=-54.8 EndY=20 EndZ=0
    g5: LineSegment [constr] StartX=-54.8 StartY=20 StartZ=0 EndX=54.8 EndY=20 EndZ=0
    g6: LineSegment StartX=34.8 StartY=162.959 StartZ=0 EndX=-34.8 EndY=162.959 EndZ=0
    g7: LineSegment StartX=-34.8 StartY=162.959 StartZ=0 EndX=-34.8 EndY=149.512 EndZ=0
    g8: LineSegment StartX=-34.8 StartY=149.512 StartZ=0 EndX=34.8 EndY=149.512 EndZ=0
    g9: LineSegment StartX=34.8 StartY=149.512 StartZ=0 EndX=34.8 EndY=162.959 EndZ=0
    g10: LineSegment StartX=34.8 StartY=107.062 StartZ=0 EndX=-34.8 EndY=107.062 EndZ=0
    g11: LineSegment StartX=-34.8 StartY=107.062 StartZ=0 EndX=-34.8 EndY=134.512 EndZ=0
    g12: LineSegment StartX=-34.8 StartY=134.512 StartZ=0 EndX=34.8 EndY=134.512 EndZ=0
    g13: LineSegment StartX=34.8 StartY=134.512 StartZ=0 EndX=34.8 EndY=107.062 EndZ=0
    g14: LineSegment StartX=34.8 StartY=239 StartZ=0 EndX=-34.8 EndY=239 EndZ=0
    g15: LineSegment StartX=-34.8 StartY=239 StartZ=0 EndX=-34.8 EndY=220.485 EndZ=0
    g16: LineSegment StartX=-34.8 StartY=220.485 StartZ=0 EndX=34.8 EndY=220.485 EndZ=0
    g17: LineSegment StartX=34.8 StartY=220.485 StartZ=0 EndX=34.8 EndY=239 EndZ=0
    g18: LineSegment StartX=34.8 StartY=182.959 StartZ=0 EndX=-34.8 EndY=182.959 EndZ=0
    g19: LineSegment StartX=-34.8 StartY=182.959 StartZ=0 EndX=-34.8 EndY=205.485 EndZ=0
    g20: LineSegment StartX=-34.8 StartY=205.485 StartZ=0 EndX=34.8 EndY=205.485 EndZ=0
    g21: LineSegment StartX=34.8 StartY=205.485 StartZ=0 EndX=34.8 EndY=182.959 EndZ=0
    g22: LineSegment StartX=-34.8 StartY=81.9803 StartZ=0 EndX=-34.8 EndY=59.2632 EndZ=0
    g23: LineSegment StartX=-34.8 StartY=59.2632 StartZ=0 EndX=34.8 EndY=59.2632 EndZ=0
    g24: LineSegment StartX=34.8 StartY=59.2632 StartZ=0 EndX=34.8 EndY=81.9803 EndZ=0
    g25: LineSegment StartX=34.8 StartY=81.9803 StartZ=0 EndX=-34.8 EndY=81.9803 EndZ=0
    g26: LineSegment StartX=-34.8 StartY=44.2632 StartZ=0 EndX=-34.8 EndY=15 EndZ=0
    g27: LineSegment StartX=-34.8 StartY=15 StartZ=0 EndX=34.8 EndY=15 EndZ=0
    g28: LineSegment StartX=34.8 StartY=15 StartZ=0 EndX=34.8 EndY=44.2632 EndZ=0
    g29: LineSegment StartX=34.8 StartY=44.2632 StartZ=0 EndX=-34.8 EndY=44.2632 EndZ=0
    g30: LineSegment StartX=54.8 StartY=20 StartZ=0 EndX=54.8 EndY=256.6 EndZ=0
    g31: LineSegment [constr] StartX=-54.8 StartY=256.6 StartZ=0 EndX=54.8 EndY=256.6 EndZ=0
    g32: LineSegment StartX=-54.8 StartY=20 StartZ=0 EndX=-54.8 EndY=0 EndZ=0
    g33: LineSegment StartX=-54.8 StartY=0 StartZ=0 EndX=54.8 EndY=0 EndZ=0
    g34: LineSegment StartX=54.8 StartY=0 StartZ=0 EndX=54.8 EndY=20 EndZ=0
    g35: LineSegment [constr] StartX=54.8 StartY=20 StartZ=0 EndX=-54.8 EndY=20 EndZ=0
    g36: LineSegment StartX=-54.8 StartY=256.6 StartZ=0 EndX=-54.8 EndY=259 EndZ=0
    g37: LineSegment StartX=-54.8 StartY=259 StartZ=0 EndX=54.8 EndY=259 EndZ=0
    g38: LineSegment StartX=54.8 StartY=259 StartZ=0 EndX=54.8 EndY=256.6 EndZ=0
    g39: Circle CenterX=-44.8 CenterY=30 CenterZ=0 NormalX=0 NormalY=0 NormalZ=1 AngleXU=0 Radius=0.855
    g40: Circle CenterX=44.8 CenterY=30 CenterZ=0 NormalX=0 NormalY=0 NormalZ=1 AngleXU=0 Radius=0.855
    g41: Circle CenterX=-44.8 CenterY=112 CenterZ=0 NormalX=0 NormalY=0 NormalZ=1 AngleXU=0 Radius=0.855
    g42: Circle CenterX=44.8 CenterY=112 CenterZ=0 NormalX=0 NormalY=0 NormalZ=1 AngleXU=0 Radius=0.855
    g43: Circle CenterX=-44.8 CenterY=157 CenterZ=0 NormalX=0 NormalY=0 NormalZ=1 AngleXU=0 Radius=0.855
    g44: Circle CenterX=44.8 CenterY=157 CenterZ=0 NormalX=0 NormalY=0 NormalZ=1 AngleXU=0 Radius=0.855
    g45: Circle CenterX=-44.8 CenterY=135 CenterZ=0 NormalX=0 NormalY=0 NormalZ=1 AngleXU=0 Radius=0.855
    g46: Circle CenterX=44.8 CenterY=135 CenterZ=0 NormalX=0 NormalY=0 NormalZ=1 AngleXU=0 Radius=0.855
    g47: Circle CenterX=-44.8 CenterY=230 CenterZ=0 NormalX=0 NormalY=0 NormalZ=1 AngleXU=0 Radius=0.855
    g48: Circle CenterX=44.8 CenterY=230 CenterZ=0 NormalX=0 NormalY=0 NormalZ=1 AngleXU=0 Radius=0.855
    g49: LineSegment StartX=-34.8 StartY=89.607 StartZ=0 EndX=34.8 EndY=89.607 EndZ=0
    g50: LineSegment StartX=34.8 StartY=89.607 StartZ=0 EndX=34.8 EndY=98.0817 EndZ=0
    g51: LineSegment StartX=34.8 StartY=98.0817 StartZ=0 EndX=-34.8 EndY=98.0817 EndZ=0
    g52: LineSegment StartX=-34.8 StartY=98.0817 StartZ=0 EndX=-34.8 EndY=89.607 EndZ=0
    g53: Circle CenterX=-44.8 CenterY=94 CenterZ=0 NormalX=0 NormalY=0 NormalZ=1 AngleXU=0 Radius=0.855
    g54: Circle CenterX=44.8 CenterY=94 CenterZ=0 NormalX=0 NormalY=0 NormalZ=1 AngleXU=0 Radius=0.85
  constraints (151):
    c: Coincident(g0,g1)
    c: Coincident(g1,g2)
    c: Coincident(g2,g3)
    c: Coincident(g3,g0)
    c: Horizontal(g2)
    c: Vertical(g1)
    c: Vertical(g3)
    c: DistanceY(g0,g2) = 228.6
    c: DistanceX(g0,g0) = 101.6
    c: DistanceX(g0,g-1) = 50.8
    c: Coincident(g4,g5)
    c: Vertical(g4)
    c: Horizontal(g5)
    c: DistanceX(g4,g0) = 4
    c: Horizontal(g0)
    c: Coincident(g6,g7)
    c: Coincident(g7,g8)
    c: Coincident(g8,g9)
    c: Coincident(g9,g6)
    c: Horizontal(g6)
    c: Horizontal(g8)
    c: Vertical(g7)
    c: Vertical(g9)
    c: Coincident(g10,g11)
    c: Coincident(g11,g12)
    c: Coincident(g12,g13)
    c: Coincident(g13,g10)
    c: Horizontal(g10)
    c: Horizontal(g12)
    c: Vertical(g11)
    c: Vertical(g13)
    c: Coincident(g14,g15)
    c: Coincident(g15,g16)
    c: Coincident(g16,g17)
    c: Coincident(g17,g14)
    c: Horizontal(g14)
    c: Horizontal(g16)
    c: Vertical(g15)
    c: Vertical(g17)
    c: Coincident(g18,g19)
    c: Coincident(g19,g20)
    c: Coincident(g20,g21)
    c: Coincident(g21,g18)
    c: Horizontal(g18)
    c: Horizontal(g20)
    c: Vertical(g19)
    c: DistanceY(g20,g16) = 15
    c: Vertical(g12,g18)
    c: DistanceY(g6,g18) = 20
    c: Coincident(g22,g23)
    c: Coincident(g23,g24)
    c: Coincident(g24,g25)
    c: Coincident(g25,g22)
    c: Vertical(g22)
    c: Vertical(g24)
    c: Horizontal(g23)
    c: Horizontal(g25)
    c: Coincident(g26,g27)
    c: Coincident(g27,g28)
    c: Coincident(g28,g29)
    c: Coincident(g29,g26)
    c: Vertical(g26)
    c: Vertical(g28)
    c: Horizontal(g27)
    c: Horizontal(g29)
    c: DistanceY(g26,g22) = 15
    c: Vertical(g22,g26)
    c: Vertical(g10,g24)
    c: Vertical(g24,g28)
    c: Coincident(g30,g5)
    c: Vertical(g30)
    c: DistanceY(g1,g30) = 4
    c: Horizontal(g4,g30)
    c: Coincident(g31,g4)
    c: Coincident(g31,g30)
    c: DistanceX(g4,g5) = 109.6
    c: DistanceY(g-1,g5) = 20
    c: Coincident(g32,g33)
    c: Coincident(g33,g34)
    c: Coincident(g34,g35)
    c: Coincident(g35,g32)
    c: Vertical(g32)
    c: Vertical(g34)
    c: Horizontal(g33)
    c: Horizontal(g35)
    c: Coincident(g32,g4)
    c: Horizontal(g33,g-1)
    c: Vertical(g34,g5)
    c: Vertical(g21)
    c: Coincident(g36,g4)
    c: Vertical(g36)
    c: Coincident(g37,g36)
    c: Horizontal(g37)
    c: Coincident(g38,g37)
    c: Coincident(g38,g30)
    c: Vertical(g38)
    c: DistanceY(g-1,g26) = 15
    c: DistanceX(g32,g26) = 20
    c: DistanceX(g27,g33) = 20
    c: Vertical(g10,g22)
    c: Vertical(g11,g7)
    c: Vertical(g6,g18)
    c: Vertical(g19,g15)
    c: Vertical(g12,g8)
    c: Vertical(g20,g16)
    c: DistanceY(g12,g8) = 15
    c: DistanceY(g33,g37) = 259
    c: Diameter(g39) = 1.71
    c: Diameter(g40) = 1.71
    c: Horizontal(g40,g39)
    c: DistanceX(g4,g39) = 10
    c: DistanceX(g40,g5) = 10
    c: Diameter(g41) = 1.71
    c: Diameter(g42) = 1.71
    c: Horizontal(g42,g41)
    c: Diameter(g43) = 1.71
    c: Diameter(g44) = 1.71
    c: Horizontal(g44,g43)
    c: Vertical(g43,g39)
    c: Vertical(g44,g42)
    c: Diameter(g45) = 1.71
    c: Diameter(g46) = 1.71
    c: Horizontal(g46,g45)
    c: DistanceY(g-1,g39) = 30
    c: DistanceY(g-1,g41) = 112
    c: Vertical(g45,g41)
    c: DistanceY(g-1,g45) = 135
    c: DistanceY(g-1,g43) = 157
    c: Vertical(g42,g46)
    c: Diameter(g48) = 1.71
    c: Diameter(g47) = 1.71
    c: Vertical(g48,g44)
    c: Vertical(g47,g43)
    c: DistanceY(g-1,g47) = 230
    c: Horizontal(g48,g47)
    c: Coincident(g49,g50)
    c: Coincident(g50,g51)
    c: Coincident(g51,g52)
    c: Coincident(g52,g49)
    c: Horizontal(g49)
    c: Horizontal(g51)
    c: Vertical(g50)
    c: Vertical(g52)
    c: Vertical(g49,g22)
    c: Vertical(g49,g24)
    c: Diameter(g53) = 1.71
    c: Vertical(g41,g53)
    c: Diameter(g54) = 1.7
    c: Horizontal(g53,g54)
    c: Vertical(g54,g42)
    c: DistanceY(g-1,g53) = 94
FEATURE [PartDesign::Pad] Pad004  label="Frontplate Pad"
  Direction = (0,-1,2e-16)
  Length = 3
  Length2 = 10
  Placement = pos=(0,0,0) rot=(1,0,0;1.5708rad)
  Profile = -> Sketch005
  ReferenceAxis = -> Sketch005 [N_Axis]
  Reversed = true
  Suppressed = false
  Type = 0
  expr: Length = <<Monitor Chassis Parameters>>.GSBackPlateThickness
FEATURE [Sketcher::SketchObject] Sketch007  label="Frontplate Foot Sketch"
  ArcFitTolerance = 1e-06
  AttachmentSupport = -> [XZ_Plane002]
  FullyConstrained = true
  MakeInternals = false
  MapMode = 5
  Placement = pos=(0,0,0) rot=(1,0,0;1.5708rad)
  expr: Constraints[11] = <<Monitor Chassis Parameters>>.GSTowerFeetThickness
  expr: Constraints[21] = <<Monitor Chassis Parameters>>.GSTowerFeetThickness
  expr: Constraints[22] = <<Monitor Chassis Parameters>>.GSBackPlateFootWidth
  expr: Constraints[23] = 0.5 * <<Monitor Chassis Parameters>>.GSBackPlateWidth
  expr: Constraints[8] = <<Monitor Chassis Parameters>>.GSBackPlateFootWidth
  expr: Constraints[9] = 0.5 * <<Monitor Chassis Parameters>>.GSBackPlateWidth
  sketch-geometry (8):
    g0: LineSegment StartX=-54.8 StartY=-5 StartZ=0 EndX=-19.8 EndY=-5 EndZ=0
    g1: LineSegment StartX=-19.8 StartY=-5 StartZ=0 EndX=-19.8 EndY=0 EndZ=0
    g2: LineSegment StartX=-19.8 StartY=0 StartZ=0 EndX=-54.8 EndY=0 EndZ=0
    g3: LineSegment StartX=-54.8 StartY=0 StartZ=0 EndX=-54.8 EndY=-5 EndZ=0
    g4: LineSegment StartX=54.8 StartY=-5 StartZ=0 EndX=54.8 EndY=0 EndZ=0
    g5: LineSegment StartX=54.8 StartY=0 StartZ=0 EndX=19.8 EndY=0 EndZ=0
    g6: LineSegment StartX=19.8 StartY=0 StartZ=0 EndX=19.8 EndY=-5 EndZ=0
    g7: LineSegment StartX=19.8 StartY=-5 StartZ=0 EndX=54.8 EndY=-5 EndZ=0
  constraints (24):
    c: Coincident(g0,g1)
    c: Coincident(g1,g2)
    c: Coincident(g2,g3)
    c: Coincident(g3,g0)
    c: Horizontal(g0)
    c: Horizontal(g2)
    c: Vertical(g1)
    c: Vertical(g3)
    c: DistanceX(g2,g1) = 35
    c: DistanceX(g2,g-1) = 54.8
    c: Horizontal(g2,g-1)
    c: DistanceY(g0,g2) = 5
    c: Coincident(g4,g5)
    c: Coincident(g5,g6)
    c: Coincident(g6,g7)
    c: Coincident(g7,g4)
    c: Vertical(g4)
    c: Vertical(g6)
    c: Horizontal(g5)
    c: Horizontal(g7)
    c: Horizontal(g5,g-1)
    c: DistanceY(g4,g4) = 5
    c: DistanceX(g6,g4) = 35
    c: DistanceX(g-1,g4) = 54.8
FEATURE [PartDesign::Pad] Pad006  label="Frontplate Foot Pad"
  BaseFeature = -> Pad004
  Direction = (0,-1,2e-16)
  Length = 65
  Length2 = 3
  Placement = pos=(0,0,0) rot=(1,0,0;1.5708rad)
  Profile = -> Sketch007
  ReferenceAxis = -> Sketch007 [N_Axis]
  Suppressed = false
  Type = 4
  expr: Length = <<Monitor Chassis Parameters>>.GSBackPlateFootLengthForward
  expr: Length2 = <<Monitor Chassis Parameters>>.GSBackPlateThickness
FEATURE [Sketcher::SketchObject] Sketch008  label="Frontplate Foot Screw Holes Sketch"
  ArcFitTolerance = 1e-06
  AttachmentSupport = -> [XY_Plane002]
  FullyConstrained = true
  MakeInternals = false
  MapMode = 5
  expr: Constraints[0] = <<Monitor Chassis Parameters>>.GSBackPlateFootScrewHoleForwardOffset
  expr: Constraints[1] = 0.5 * <<Monitor Chassis Parameters>>.GSBackPlateWidth - 0.5 * <<Monitor Chassis Parameters>>.GSBackPlateFootWidth
  expr: Constraints[2] = 0.5 * <<Monitor Chassis Parameters>>.GSBackPlateWidth - 0.5 * <<Monitor Chassis Parameters>>.GSBackPlateFootWidth
  expr: Constraints[3] = <<Monitor Chassis Parameters>>.GSTowerFeetScrewDiameter
  expr: Constraints[4] = <<Monitor Chassis Parameters>>.GSTowerFeetScrewDiameter
  sketch-geometry (2):
    g0: Circle CenterX=-37.3 CenterY=-55 CenterZ=0 NormalX=0 NormalY=0 NormalZ=1 AngleXU=0 Radius=1.7
    g1: Circle CenterX=37.3 CenterY=-55 CenterZ=0 NormalX=0 NormalY=0 NormalZ=1 AngleXU=0 Radius=1.7
  constraints (6):
    c: DistanceY(g0,g-1) = 55
    c: DistanceX(g0,g-1) = 37.3
    c: DistanceX(g-1,g1) = 37.3
    c: Diameter(g0) = 3.4
    c: Diameter(g1) = 3.4
    c: Horizontal(g1,g0)
FEATURE [PartDesign::Hole] Hole001  label="Frontplate Foot Screw Holes"
  BaseFeature = -> Pad006
  CustomThreadClearance = 0
  Depth = 25
  DepthType = 0
  Diameter = 3.4
  DrillForDepth = false
  DrillPoint = 1
  DrillPointAngle = 118
  HoleCutCountersinkAngle = 90
  HoleCutCustomValues = false
  HoleCutDepth = 0
  HoleCutDiameter = 8
  HoleCutType = 2
  ModelThread = false
  Placement = pos=(0,0,0) rot=(1,0,0;1.5708rad)
  Profile = -> Sketch008
  Suppressed = false
  Tapered = false
  TaperedAngle = 90
  ThreadClass = 0
  ThreadDepth = 25
  ThreadDepthType = 0
  ThreadDirection = 0
  ThreadFit = 0
  ThreadSize = 0
  ThreadType = 0
  Threaded = false
  UseCustomThreadClearance = false
  expr: Diameter = <<Monitor Chassis Parameters>>.GSTowerFeetScrewDiameter
  expr: HoleCutDiameter = <<Monitor Chassis Parameters>>.GSM4BoltCountersinkDiameter
FEATURE [Sketcher::SketchObject] Sketch009  label="Frontplate Foot Support Corner Sketch"
  ArcFitTolerance = 1e-06
  AttachmentSupport = -> [DatumPlane001]
  FullyConstrained = true
  MakeInternals = false
  MapMode = 5
  Placement = pos=(54.8,0,0) rot=(0.57735,0.57735,0.57735;2.0944rad)
  expr: Constraints[1] = <<Monitor Chassis Parameters>>.GSBackPlateThickness
  expr: Constraints[24] = 0.8 * <<Monitor Chassis Parameters>>.GSTowerFloorDepth
  expr: Constraints[25] = 0.6 * <<Monitor Chassis Parameters>>.GSTowerFloorDepth
  expr: Constraints[26] = <<Monitor Chassis Parameters>>.GSSideCornerCutoutInset
  expr: Constraints[27] = <<Monitor Chassis Parameters>>.GSSideCornerCutoutInset
  expr: Constraints[28] = 2 * <<Monitor Chassis Parameters>>.GSSideCornerCutoutInset
  expr: Constraints[29] = 3 * <<Monitor Chassis Parameters>>.GSSideCornerCutoutInset
  expr: Constraints[39] = 0.8 * <<Monitor Chassis Parameters>>.GSTowerFloorDepth
  expr: Constraints[3] = <<Monitor Chassis Parameters>>.GSTowerFeetThickness
  expr: Constraints[41] = <<Monitor Chassis Parameters>>.GSSideCornerCutoutInset
  expr: Constraints[42] = -2 * <<Monitor Chassis Parameters>>.GSSideCornerCutoutInset
  expr: Constraints[43] = 3 * <<Monitor Chassis Parameters>>.GSSideCornerCutoutInset
  expr: Constraints[54] = 0.8 * <<Monitor Chassis Parameters>>.GSTowerFloorDepth
  expr: Constraints[55] = 0.6 * <<Monitor Chassis Parameters>>.GSTowerFloorDepth
  expr: Constraints[56] = <<Monitor Chassis Parameters>>.GSSideCornerCutoutInset
  expr: Constraints[57] = <<Monitor Chassis Parameters>>.GSSideCornerCutoutInset
  expr: Constraints[58] = 2 * <<Monitor Chassis Parameters>>.GSSideCornerCutoutInset
  expr: Constraints[59] = 3 * <<Monitor Chassis Parameters>>.GSSideCornerCutoutInset
  expr: Constraints[62] = <<Monitor Chassis Parameters>>.GSTowerThirdFloorHeight
  expr: Constraints[63] = <<Monitor Chassis Parameters>>.GSTowerSecondFloorHeight
  expr: Constraints[64] = 0.6 * <<Monitor Chassis Parameters>>.GSTowerFloorDepth
  expr: Constraints[65] = <<Monitor Chassis Parameters>>.GSTowerFourthFloorHeight + <<Monitor Chassis Parameters>>.GSTowerFloorThickness
  expr: Constraints[6] = 0.8 * <<Monitor Chassis Parameters>>.GSTowerFloorDepth
  expr: Constraints[70] = 2 * <<Monitor Chassis Parameters>>.GSSideCornerCutoutInset
  expr: Constraints[71] = 3 * <<Monitor Chassis Parameters>>.GSSideCornerCutoutInset
  expr: Constraints[73] = <<Monitor Chassis Parameters>>.GSSideCornerCutoutInset
  expr: Constraints[7] = 0.6 * <<Monitor Chassis Parameters>>.GSTowerFloorDepth
  sketch-geometry (24):
    g0: LineSegment StartX=-41 StartY=-5 StartZ=0 EndX=3 EndY=-5 EndZ=0
    g1: LineSegment StartX=3 StartY=28 StartZ=0 EndX=3 EndY=-5 EndZ=0
    g2: LineSegment StartX=-41 StartY=-5 StartZ=0 EndX=3 EndY=28 EndZ=0
    g3: LineSegment StartX=-23 StartY=171 StartZ=0 EndX=-3 EndY=186 EndZ=0
    g4: LineSegment StartX=-3 StartY=186 StartZ=0 EndX=-3 EndY=171 EndZ=0
    g5: LineSegment StartX=-23 StartY=171 StartZ=0 EndX=-3 EndY=171 EndZ=0
    g6: LineSegment StartX=3 StartY=198 StartZ=0 EndX=3 EndY=165 EndZ=0
    g7: LineSegment StartX=3 StartY=165 StartZ=0 EndX=-41 EndY=165 EndZ=0
    g8: LineSegment StartX=-41 StartY=165 StartZ=0 EndX=3 EndY=198 EndZ=0
    g9: LineSegment StartX=-23 StartY=1 StartZ=0 EndX=-3 EndY=16 EndZ=0
    g10: LineSegment StartX=-3 StartY=16 StartZ=0 EndX=-3 EndY=1 EndZ=0
    g11: LineSegment StartX=-23 StartY=1 StartZ=0 EndX=-3 EndY=1 EndZ=0
    g12: LineSegment StartX=-23 StartY=253 StartZ=0 EndX=-3 EndY=238 EndZ=0
    g13: LineSegment StartX=-3 StartY=238 StartZ=0 EndX=-3 EndY=253 EndZ=0
    g14: LineSegment StartX=-23 StartY=253 StartZ=0 EndX=-3 EndY=253 EndZ=0
    g15: LineSegment StartX=3 StartY=226 StartZ=0 EndX=3 EndY=259 EndZ=0
    g16: LineSegment StartX=3 StartY=259 StartZ=0 EndX=-41 EndY=259 EndZ=0
    g17: LineSegment StartX=-41 StartY=259 StartZ=0 EndX=3 EndY=226 EndZ=0
    g18: LineSegment StartX=-23 StartY=91 StartZ=0 EndX=-3 EndY=106 EndZ=0
    g19: LineSegment StartX=-3 StartY=106 StartZ=0 EndX=-3 EndY=91 EndZ=0
    g20: LineSegment StartX=-23 StartY=91 StartZ=0 EndX=-3 EndY=91 EndZ=0
    g21: LineSegment StartX=3 StartY=118 StartZ=0 EndX=3 EndY=85 EndZ=0
    g22: LineSegment StartX=3 StartY=85 StartZ=0 EndX=-41 EndY=85 EndZ=0
    g23: LineSegment StartX=-41 StartY=85 StartZ=0 EndX=3 EndY=118 EndZ=0
  constraints (74):
    c: Horizontal(g0)
    c: DistanceX(g-1,g0) = 3
    c: Vertical(g1)
    c: DistanceY(g0,g-1) = 5
    c: Coincident(g2,g0)
    c: Coincident(g2,g1)
    c: DistanceX(g0,g0) = 44
    c: DistanceY(g0,g1) = 33
    c: Coincident(g4,g3)
    c: Vertical(g4)
    c: Coincident(g5,g3)
    c: Coincident(g5,g4)
    c: Horizontal(g5)
    c: Vertical(g6)
    c: Coincident(g7,g6)
    c: Horizontal(g7)
    c: Coincident(g8,g7)
    c: Coincident(g8,g6)
    c: Coincident(g10,g9)
    c: Vertical(g10)
    c: Coincident(g11,g9)
    c: Coincident(g11,g10)
    c: Horizontal(g11)
    c: Vertical(g6,g1)
    c: DistanceX(g7,g6) = 44
    c: DistanceY(g6,g6) = 33
    c: DistanceY(g6,g4) = 6
    c: DistanceX(g4,g6) = 6
    c: DistanceY(g3,g6) = 12
    c: DistanceX(g7,g3) = 18
    c: Coincident(g13,g12)
    c: Vertical(g13)
    c: Coincident(g14,g12)
    c: Coincident(g14,g13)
    c: Horizontal(g14)
    c: Vertical(g15)
    c: Horizontal(g16)
    c: Coincident(g17,g16)
    c: Coincident(g17,g15)
    c: DistanceX(g16,g15) = 44
    c: DistanceY(g15,g13) = -6
    c: DistanceX(g13,g15) = 6
    c: DistanceY(g12,g15) = -12
    c: DistanceX(g16,g12) = 18
    c: Coincident(g19,g18)
    c: Vertical(g19)
    c: Coincident(g20,g18)
    c: Coincident(g20,g19)
    c: Horizontal(g20)
    c: Vertical(g21)
    c: Coincident(g22,g21)
    c: Horizontal(g22)
    c: Coincident(g23,g22)
    c: Coincident(g23,g21)
    c: DistanceX(g22,g21) = 44
    c: DistanceY(g21,g21) = 33
    c: DistanceY(g21,g19) = 6
    c: DistanceX(g19,g21) = 6
    c: DistanceY(g18,g21) = 12
    c: DistanceX(g22,g18) = 18
    c: Vertical(g21,g6)
    c: Vertical(g6,g15)
    c: DistanceY(g-1,g6) = 165
    c: DistanceY(g-1,g21) = 85
    c: DistanceY(g15,g15) = 33
    c: DistanceY(g-1,g15) = 259
    c: Horizontal(g16,g15)
    c: Vertical(g16,g15)
    c: Vertical(g1,g0)
    c: Horizontal(g1,g0)
    c: DistanceY(g9,g1) = 12
    c: DistanceX(g0,g9) = 18
    c: Vertical(g19,g9)
    c: DistanceY(g0,g10) = 6
FEATURE [PartDesign::Pad] Pad007  label="Frontplate Floor Support Corner Pad"
  BaseFeature = -> Hole001
  Direction = (1,0,0)
  Length = 2.5
  Length2 = 10
  Placement = pos=(0,0,0) rot=(1,0,0;1.5708rad)
  Profile = -> Sketch009
  ReferenceAxis = -> Sketch009 [N_Axis]
  Suppressed = false
  Type = 0
  expr: Length = <<Monitor Chassis Parameters>>.GSSideCornerThickness
FEATURE [PartDesign::Mirrored] Mirrored001  label="Frontplate Floor Support Corner Mirrored"
  BaseFeature = -> Pad007
  MirrorPlane = -> YZ_Plane002
  Originals = -> [Pad007]
  Placement = pos=(0,0,0) rot=(1,0,0;1.5708rad)
  Suppressed = false
  TransformMode = 0
FEATURE [Sketcher::SketchObject] Sketch010  label="Frontplate Floors Sketch"
  ArcFitTolerance = 1e-06
  AttachmentSupport = -> [DatumPlane001]
  FullyConstrained = true
  MakeInternals = false
  MapMode = 5
  Placement = pos=(54.8,0,0) rot=(0.57735,0.57735,0.57735;2.0944rad)
  expr: Constraints[10] = <<Monitor Chassis Parameters>>.GSTowerSecondFloorDepth
  expr: Constraints[21] = <<Monitor Chassis Parameters>>.GSTowerFourthFloorDepth
  expr: Constraints[32] = <<Monitor Chassis Parameters>>.GSTowerThirdFloorDepth
  expr: Constraints[43] = <<Monitor Chassis Parameters>>.GSTowerFirstFloorDepth
  expr: Constraints[44] = <<Monitor Chassis Parameters>>.GSTowerFirstFloorHeight
  expr: Constraints[45] = <<Monitor Chassis Parameters>>.GSTowerSecondFloorHeight
  expr: Constraints[46] = <<Monitor Chassis Parameters>>.GSTowerFourthFloorHeight
  expr: Constraints[47] = <<Monitor Chassis Parameters>>.GSTowerThirdFloorHeight
  expr: Constraints[9] = <<Monitor Chassis Parameters>>.GSTowerFloorThickness
  sketch-geometry (16):
    g0: LineSegment StartX=-55 StartY=85 StartZ=0 EndX=0 EndY=85 EndZ=0
    g1: LineSegment StartX=0 StartY=85 StartZ=0 EndX=0 EndY=89 EndZ=0
    g2: LineSegment StartX=0 StartY=89 StartZ=0 EndX=-55 EndY=89 EndZ=0
    g3: LineSegment StartX=-55 StartY=89 StartZ=0 EndX=-55 EndY=85 EndZ=0
    g4: LineSegment StartX=-55 StartY=255 StartZ=0 EndX=0 EndY=255 EndZ=0
    g5: LineSegment StartX=0 StartY=255 StartZ=0 EndX=0 EndY=259 EndZ=0
    g6: LineSegment StartX=0 StartY=259 StartZ=0 EndX=-55 EndY=259 EndZ=0
    g7: LineSegment StartX=-55 StartY=259 StartZ=0 EndX=-55 EndY=255 EndZ=0
    g8: LineSegment StartX=-55 StartY=165 StartZ=0 EndX=0 EndY=165 EndZ=0
    g9: LineSegment StartX=0 StartY=165 StartZ=0 EndX=0 EndY=169 EndZ=0
    g10: LineSegment StartX=0 StartY=169 StartZ=0 EndX=-55 EndY=169 EndZ=0
    g11: LineSegment StartX=-55 StartY=169 StartZ=0 EndX=-55 EndY=165 EndZ=0
    g12: LineSegment StartX=-50 StartY=5 StartZ=0 EndX=0 EndY=5 EndZ=0
    g13: LineSegment StartX=0 StartY=5 StartZ=0 EndX=0 EndY=9 EndZ=0
    g14: LineSegment StartX=0 StartY=9 StartZ=0 EndX=-50 EndY=9 EndZ=0
    g15: LineSegment StartX=-50 StartY=9 StartZ=0 EndX=-50 EndY=5 EndZ=0
  constraints (48):
    c: Coincident(g0,g1)
    c: Coincident(g1,g2)
    c: Coincident(g2,g3)
    c: Coincident(g3,g0)
    c: Horizontal(g0)
    c: Horizontal(g2)
    c: Vertical(g1)
    c: Vertical(g3)
    c: Vertical(g0,g-1)
    c: DistanceY(g0,g2) = 4
    c: DistanceX(g2,g1) = 55
    c: Coincident(g4,g5)
    c: Coincident(g5,g6)
    c: Coincident(g6,g7)
    c: Coincident(g7,g4)
    c: Horizontal(g4)
    c: Horizontal(g6)
    c: Vertical(g5)
    c: Vertical(g7)
    c: Vertical(g4,g-1)
    c: DistanceY(g4,g6) = 4
    c: DistanceX(g6,g5) = 55
    c: Coincident(g8,g9)
    c: Coincident(g9,g10)
    c: Coincident(g10,g11)
    c: Coincident(g11,g8)
    c: Horizontal(g8)
    c: Horizontal(g10)
    c: Vertical(g9)
    c: Vertical(g11)
    c: Vertical(g8,g-1)
    c: DistanceY(g8,g10) = 4
    c: DistanceX(g10,g9) = 55
    c: Coincident(g12,g13)
    c: Coincident(g13,g14)
    c: Coincident(g14,g15)
    c: Coincident(g15,g12)
    c: Horizontal(g12)
    c: Horizontal(g14)
    c: Vertical(g13)
    c: Vertical(g15)
    c: Vertical(g12,g-1)
    c: DistanceY(g12,g14) = 4
    c: DistanceX(g14,g13) = 50
    c: DistanceY(g-1,g12) = 5
    c: DistanceY(g-1,g0) = 85
    c: DistanceY(g-1,g4) = 255
    c: DistanceY(g-1,g8) = 165
FEATURE [PartDesign::Pad] Pad008  label="Tower Floors Pad"
  BaseFeature = -> Mirrored001
  Direction = (1,0,0)
  Length = 109.6
  Length2 = 10
  Placement = pos=(0,0,0) rot=(1,0,0;1.5708rad)
  Profile = -> Sketch010
  ReferenceAxis = -> Sketch010 [N_Axis]
  Reversed = true
  Suppressed = false
  Type = 0
  expr: Length = <<Monitor Chassis Parameters>>.GSBackPlateWidth
FEATURE [PartDesign::Plane] DatumPlane002  label="First Floor DatumPlane"
  AttachmentOffset = pos=(0,0,9) rot=(0,0,1;0rad)
  AttachmentSupport = -> [XY_Plane002]
  Length = 138.311
  MapMode = 5
  Placement = pos=(0,0,9) rot=(0,0,1;0rad)
  ResizeMode = 0
  Width = 146.361
  expr: .AttachmentOffset.Base.z = <<Monitor Chassis Parameters>>.GSTowerFirstFloorHeight + <<Monitor Chassis Parameters>>.GSTowerFloorThickness
FEATURE [PartDesign::Plane] DatumPlane003  label="Second Floor DatumPlane"
  AttachmentOffset = pos=(0,0,89) rot=(0,0,1;0rad)
  AttachmentSupport = -> [XY_Plane002]
  Length = 138.311
  MapMode = 5
  Placement = pos=(0,0,89) rot=(0,0,1;0rad)
  ResizeMode = 0
  Width = 146.361
  expr: .AttachmentOffset.Base.z = <<Monitor Chassis Parameters>>.GSTowerSecondFloorHeight + <<Monitor Chassis Parameters>>.GSTowerFloorThickness
FEATURE [PartDesign::Plane] DatumPlane004  label="Third Floor DatumPlane"
  AttachmentOffset = pos=(0,0,169) rot=(0,0,1;0rad)
  AttachmentSupport = -> [XY_Plane002]
  Length = 138.311
  MapMode = 5
  Placement = pos=(0,0,169) rot=(0,0,1;0rad)
  ResizeMode = 0
  Width = 146.361
  expr: .AttachmentOffset.Base.z = <<Monitor Chassis Parameters>>.GSTowerThirdFloorHeight + <<Monitor Chassis Parameters>>.GSTowerFloorThickness
FEATURE [Sketcher::SketchObject] Sketch011  label="Third Floor Holes Sketch"
  ArcFitTolerance = 1e-06
  AttachmentSupport = -> [DatumPlane004]
  FullyConstrained = true
  MakeInternals = false
  MapMode = 5
  Placement = pos=(0,0,169) rot=(0,0,1;0rad)
  expr: Constraints[1] = 0.5 * <<Monitor Chassis Parameters>>.GSTowerThirdFloorDepth
  expr: Constraints[2] = <<Monitor Chassis Parameters>>.GSMonitorFloorCameraMountHoleDiameter
  sketch-geometry (1):
    g0: Circle CenterX=0 CenterY=-27.5 CenterZ=0 NormalX=0 NormalY=0 NormalZ=1 AngleXU=0 Radius=2.75
  constraints (3):
    c: PointOnObject(g0,g-2)
    c: DistanceY(g0,g-1) = 27.5
    c: Diameter(g0) = 5.5
FEATURE [PartDesign::Pocket] Pocket  label="Third Floor Holes Pocket"
  BaseFeature = -> Pad008
  Direction = (0,0,-1)
  Length = 5
  Length2 = 5
  Placement = pos=(0,0,0) rot=(1,0,0;1.5708rad)
  Profile = -> Sketch011
  ReferenceAxis = -> Sketch011 [N_Axis]
  Suppressed = false
  Type = 0
FEATURE [Sketcher::SketchObject] Sketch012  label="Second Floor Holes Sketch"
  ArcFitTolerance = 1e-06
  AttachmentSupport = -> [DatumPlane003]
  FullyConstrained = true
  MakeInternals = false
  MapMode = 2
  Placement = pos=(0,0,89) rot=(0,0,1;0rad)
  expr: Constraints[0] = <<Monitor Chassis Parameters>>.GSMonitorFloorCameraMountHoleDiameter
  expr: Constraints[2] = 10 + 0.4 * <<Monitor Chassis Parameters>>.GSTowerSecondFloorDepth
  sketch-geometry (1):
    g0: Circle CenterX=0 CenterY=-32 CenterZ=0 NormalX=0 NormalY=0 NormalZ=1 AngleXU=0 Radius=2.75
  constraints (3):
    c: Diameter(g0) = 5.5
    c: Vertical(g-1,g0)
    c: DistanceY(g0,g-1) = 32
FEATURE [PartDesign::Pocket] Pocket001  label="Second Floor Holes Pocket"
  BaseFeature = -> Pocket
  Direction = (0,0,-1)
  Length = 5
  Length2 = 5
  Placement = pos=(0,0,0) rot=(1,0,0;1.5708rad)
  Profile = -> Sketch012
  ReferenceAxis = -> Sketch012 [N_Axis]
  Suppressed = false
  Type = 0
FEATURE [Sketcher::SketchObject] Sketch013  label="First Floor Holes Sketch"
  ArcFitTolerance = 1e-06
  AttachmentSupport = -> [DatumPlane002]
  FullyConstrained = true
  MakeInternals = false
  MapMode = 5
  Placement = pos=(0,0,9) rot=(0,0,1;0rad)
  expr: Constraints[0] = <<Monitor Chassis Parameters>>.GSMonitorFloorCameraMountHoleDiameter
  expr: Constraints[2] = 0.5 * <<Monitor Chassis Parameters>>.GSTowerFirstFloorDepth
  sketch-geometry (1):
    g0: Circle CenterX=0 CenterY=-25 CenterZ=0 NormalX=0 NormalY=0 NormalZ=1 AngleXU=0 Radius=2.75
  constraints (3):
    c: Diameter(g0) = 5.5
    c: Vertical(g0,g-1)
    c: DistanceY(g0,g-1) = 25
FEATURE [PartDesign::Pocket] Pocket002  label="First Floor Holes Pocket"
  BaseFeature = -> Pocket001
  Direction = (0,0,-1)
  Length = 5
  Length2 = 5
  Placement = pos=(0,0,0) rot=(1,0,0;1.5708rad)
  Profile = -> Sketch013
  ReferenceAxis = -> Sketch013 [N_Axis]
  Suppressed = false
  Type = 0
FEATURE [Sketcher::SketchObject] Sketch014  label="Shank Shield Riser Sketch"
  ArcFitTolerance = 1e-06
  AttachmentSupport = -> [XZ_Plane002]
  FullyConstrained = true
  MakeInternals = false
  MapMode = 5
  Placement = pos=(0,0,0) rot=(1,0,0;1.5708rad)
  expr: Constraints[0] = 3 * <<Monitor Chassis Parameters>>.GSM4TappingScrewHoleDiameter
  expr: Constraints[1] = <<Monitor Chassis Parameters>>.GSTowerFourthFloorHeight - 1.5 * <<Monitor Chassis Parameters>>.GSM4TappingScrewHoleDiameter
  expr: Constraints[2] = 0.5 * <<Monitor Chassis Parameters>>.GSBackPlateWidth - 1.5 * <<Monitor Chassis Parameters>>.GSM4TappingScrewHoleDiameter
  expr: Constraints[3] = 3 * <<Monitor Chassis Parameters>>.GSM4TappingScrewHoleDiameter
  expr: Constraints[5] = <<Monitor Chassis Parameters>>.GSBackPlateWidth - 3 * <<Monitor Chassis Parameters>>.GSM4TappingScrewHoleDiameter
  sketch-geometry (2):
    g0: Circle CenterX=-49.7 CenterY=249.9 CenterZ=0 NormalX=0 NormalY=0 NormalZ=1 AngleXU=0 Radius=5.1
    g1: Circle CenterX=49.7 CenterY=249.9 CenterZ=0 NormalX=0 NormalY=0 NormalZ=1 AngleXU=0 Radius=5.1
  constraints (6):
    c: Diameter(g0) = 10.2
    c: DistanceY(g-1,g0) = 249.9
    c: DistanceX(g0,g-1) = 49.7
    c: Diameter(g1) = 10.2
    c: Horizontal(g0,g1)
    c: DistanceX(g0,g1) = 99.4
FEATURE [PartDesign::Pad] Pad009  label="Shank Shield Riser Pad"
  BaseFeature = -> Pocket002
  Direction = (0,-1,2e-16)
  Length = 97.65
  Length2 = 10
  Placement = pos=(0,0,0) rot=(1,0,0;1.5708rad)
  Profile = -> Sketch014
  ReferenceAxis = -> Sketch014 [N_Axis]
  Suppressed = false
  Type = 0
  expr: Length = 1 + <<Monitor Chassis Parameters>>.GSBasePowerBoxTowerBackOffsetFromFront - <<Monitor Chassis Parameters>>.GSShankShieldThickness - <<Monitor Chassis Parameters>>.GSBackPlateThickness - <<Monitor Chassis Parameters>>.GSBasePowerBoxSideThickness
FEATURE [PartDesign::Plane] DatumPlane005  label="Shank Shield Riser Front DatumPlane005"
  AttachmentSupport = -> [Pad009]
  Length = 150.681
  MapMode = 5
  Placement = pos=(0,-97.65,0) rot=(1,0,0;1.5708rad)
  ResizeMode = 0
  Width = 320.081
FEATURE [Sketcher::SketchObject] Sketch015  label="Shank Shield Riser Screw Holes Sketch"
  ArcFitTolerance = 1e-06
  AttachmentSupport = -> [DatumPlane005]
  FullyConstrained = true
  MakeInternals = false
  MapMode = 5
  Placement = pos=(0,-97.65,0) rot=(1,0,0;1.5708rad)
  expr: Constraints[0] = 0.5 * <<Monitor Chassis Parameters>>.GSBackPlateWidth - 1.5 * <<Monitor Chassis Parameters>>.GSM4TappingScrewHoleDiameter
  expr: Constraints[1] = <<Monitor Chassis Parameters>>.GSM4TappingScrewHoleDiameter
  expr: Constraints[3] = <<Monitor Chassis Parameters>>.GSTowerFourthFloorHeight - 1.5 * <<Monitor Chassis Parameters>>.GSM4TappingScrewHoleDiameter
  expr: Constraints[4] = 0.5 * <<Monitor Chassis Parameters>>.GSBackPlateWidth - 1.5 * <<Monitor Chassis Parameters>>.GSM4TappingScrewHoleDiameter
  expr: Constraints[5] = <<Monitor Chassis Parameters>>.GSM4TappingScrewHoleDiameter
  sketch-geometry (2):
    g0: Circle CenterX=-49.7 CenterY=249.9 CenterZ=0 NormalX=0 NormalY=0 NormalZ=1 AngleXU=0 Radius=1.7
    g1: Circle CenterX=49.7 CenterY=249.9 CenterZ=0 NormalX=0 NormalY=0 NormalZ=1 AngleXU=0 Radius=1.7
  constraints (6):
    c: DistanceX(g0,g-1) = 49.7
    c: Diameter(g0) = 3.4
    c: Horizontal(g0,g1)
    c: DistanceY(g-1,g0) = 249.9
    c: DistanceX(g-1,g1) = 49.7
    c: Diameter(g1) = 3.4
FEATURE [PartDesign::Pocket] Pocket003  label="Shank Shield Riser Screw Holes Pocket"
  BaseFeature = -> Pad009
  Direction = (0,1,-2e-16)
  Length = 14
  Length2 = 5
  Placement = pos=(0,0,0) rot=(1,0,0;1.5708rad)
  Profile = -> Sketch015
  ReferenceAxis = -> Sketch015 [N_Axis]
  Suppressed = false
  Type = 0
  expr: Length = 14
FEATURE [PartDesign::Plane] DatumPlane006  label="Fourth Floor DatumPlane"
  AttachmentOffset = pos=(0,0,259) rot=(0,0,1;0rad)
  AttachmentSupport = -> [XY_Plane002]
  Length = 138.311
  MapMode = 5
  Placement = pos=(0,0,259) rot=(0,0,1;0rad)
  ResizeMode = 0
  Width = 146.361
  expr: .AttachmentOffset.Base.z = <<Monitor Chassis Parameters>>.GSTowerFourthFloorHeight + <<Monitor Chassis Parameters>>.GSTowerFloorThickness
FEATURE [Sketcher::SketchObject] Sketch016  label="Fourth Floor Cutout Sketch"
  ArcFitTolerance = 1e-06
  AttachmentSupport = -> [DatumPlane006]
  FullyConstrained = false
  MakeInternals = false
  MapMode = 5
  Placement = pos=(0,0,259) rot=(0,0,1;0rad)
  sketch-geometry (4):
    g0: LineSegment StartX=-44.9421 StartY=-8.20433 StartZ=0 EndX=-44.9421 EndY=-45.1974 EndZ=0
    g1: LineSegment StartX=-44.9421 StartY=-45.1974 StartZ=0 EndX=49.6477 EndY=-45.1974 EndZ=0
    g2: LineSegment StartX=49.6477 StartY=-45.1974 StartZ=0 EndX=49.6477 EndY=-8.20433 EndZ=0
    g3: LineSegment StartX=49.6477 StartY=-8.20433 StartZ=0 EndX=-44.9421 EndY=-8.20433 EndZ=0
  constraints (8):
    c: Coincident(g0,g1)
    c: Coincident(g1,g2)
    c: Coincident(g2,g3)
    c: Coincident(g3,g0)
    c: Vertical(g0)
    c: Vertical(g2)
    c: Horizontal(g1)
    c: Horizontal(g3)
FEATURE [PartDesign::Plane] DatumPlane007  label="Suggested Backplate Split DatumPlane"
  AttachmentOffset = pos=(0,0,102) rot=(0,0,1;0rad)
  AttachmentSupport = -> [XY_Plane001]
  Length = 130.764
  MapMode = 5
  Placement = pos=(0,0,102) rot=(0,0,1;0rad)
  ResizeMode = 0
  Width = 73.1644
  expr: .AttachmentOffset.Base.z = 102
FEATURE [PartDesign::Plane] DatumPlane008  label="Suggested Frontplate Split DatumPlane"
  AttachmentOffset = pos=(0,0,145) rot=(0,0,1;0rad)
  AttachmentSupport = -> [XY_Plane002]
  Length = 138.311
  MapMode = 5
  Placement = pos=(0,0,145) rot=(0,0,1;0rad)
  ResizeMode = 0
  Width = 146.361
FEATURE [PartDesign::Body] Body001  label="Frontplate Body"
  AllowCompound = false
  Group = -> [Sketch005,Pad004,Sketch007,Pad006,Sketch008,Hole001,DatumPlane001,Sketch009,Pad007,Mirrored001,Sketch010,Pad008,DatumPlane002,DatumPlane003,DatumPlane004,Sketch011,Pocket,Sketch012,Pocket001,Sketch013,Pocket002,Sketch014,Pad009,DatumPlane005,Sketch015,Pocket003,DatumPlane006,Sketch016,DatumPlane008]
  Origin = -> Origin002
  Placement = pos=(0.1,5,0) rot=(0,0,1;3.14159rad)
  Tip = -> Pocket003
FEATURE [Sketcher::SketchObject] Sketch017  label="Tower Layer Join Screw Holes Sketch"
  ArcFitTolerance = 1e-06
  AttachmentSupport = -> [XZ_Plane001]
  FullyConstrained = true
  MakeInternals = false
  MapMode = 5
  Placement = pos=(0,0,0) rot=(1,0,0;1.5708rad)
  expr: Constraints[0] = <<Monitor Chassis Parameters>>.GSTowerLayerJoinScrewDiameter
  expr: Constraints[1] = <<Monitor Chassis Parameters>>.GSM2TappingScrewHoleDiameter
  expr: Constraints[22] = 0.5 * <<Monitor Chassis Parameters>>.GSBackPlateWidth - <<Monitor Chassis Parameters>>.GSTowerLayerJoinScrewInset
  expr: Constraints[23] = 0.5 * <<Monitor Chassis Parameters>>.GSBackPlateWidth - <<Monitor Chassis Parameters>>.GSTowerLayerJoinScrewInset
  expr: Constraints[24] = <<Monitor Chassis Parameters>>.GSTowerLayerJoinScrewHeightFromFoot_1
  expr: Constraints[25] = <<Monitor Chassis Parameters>>.GSTowerLayerJoinScrewHeightFromFoot_2
  expr: Constraints[26] = <<Monitor Chassis Parameters>>.GSTowerLayerJoinScrewHeightFromFoot_3
  expr: Constraints[27] = <<Monitor Chassis Parameters>>.GSTowerLayerJoinScrewHeightFromFoot_4
  expr: Constraints[28] = <<Monitor Chassis Parameters>>.GSTowerLayerJoinScrewHeightFromFoot_5
  expr: Constraints[29] = <<Monitor Chassis Parameters>>.GSM2TappingScrewHoleDiameter
  expr: Constraints[2] = <<Monitor Chassis Parameters>>.GSM2TappingScrewHoleDiameter
  expr: Constraints[30] = <<Monitor Chassis Parameters>>.GSM2TappingScrewHoleDiameter
  expr: Constraints[35] = <<Monitor Chassis Parameters>>.GSTowerLayerJoinScrewHeightFromFoot_6
  expr: Constraints[3] = <<Monitor Chassis Parameters>>.GSM2TappingScrewHoleDiameter
  expr: Constraints[4] = <<Monitor Chassis Parameters>>.GSM2TappingScrewHoleDiameter
  expr: Constraints[5] = <<Monitor Chassis Parameters>>.GSM2TappingScrewHoleDiameter
  expr: Constraints[6] = <<Monitor Chassis Parameters>>.GSM2TappingScrewHoleDiameter
  expr: Constraints[7] = <<Monitor Chassis Parameters>>.GSM2TappingScrewHoleDiameter
  expr: Constraints[8] = <<Monitor Chassis Parameters>>.GSM2TappingScrewHoleDiameter
  expr: Constraints[9] = <<Monitor Chassis Parameters>>.GSM2TappingScrewHoleDiameter
  sketch-geometry (12):
    g0: Circle CenterX=44.8 CenterY=157 CenterZ=0 NormalX=0 NormalY=0 NormalZ=1 AngleXU=0 Radius=0.855
    g1: Circle CenterX=-44.8 CenterY=135 CenterZ=0 NormalX=0 NormalY=0 NormalZ=1 AngleXU=0 Radius=0.855
    g2: Circle CenterX=44.8 CenterY=135 CenterZ=0 NormalX=0 NormalY=0 NormalZ=1 AngleXU=0 Radius=0.855
    g3: Circle CenterX=-44.8 CenterY=112 CenterZ=0 NormalX=0 NormalY=0 NormalZ=1 AngleXU=0 Radius=0.855
    g4: Circle CenterX=-44.8 CenterY=94 CenterZ=0 NormalX=0 NormalY=0 NormalZ=1 AngleXU=0 Radius=0.855
    g5: Circle CenterX=44.8 CenterY=112 CenterZ=0 NormalX=0 NormalY=0 NormalZ=1 AngleXU=0 Radius=0.855
    g6: Circle CenterX=44.8 CenterY=94 CenterZ=0 NormalX=0 NormalY=0 NormalZ=1 AngleXU=0 Radius=0.855
    g7: Circle CenterX=-44.8 CenterY=30 CenterZ=0 NormalX=0 NormalY=0 NormalZ=1 AngleXU=0 Radius=0.855
    g8: Circle CenterX=44.8 CenterY=30 CenterZ=0 NormalX=0 NormalY=0 NormalZ=1 AngleXU=0 Radius=0.855
    g9: Circle CenterX=-44.8 CenterY=157 CenterZ=0 NormalX=0 NormalY=0 NormalZ=1 AngleXU=0 Radius=0.855
    g10: Circle CenterX=-44.8 CenterY=230 CenterZ=0 NormalX=0 NormalY=0 NormalZ=1 AngleXU=0 Radius=0.855
    g11: Circle CenterX=44.8 CenterY=230 CenterZ=0 NormalX=0 NormalY=0 NormalZ=1 AngleXU=0 Radius=0.855
  constraints (36):
    c: Diameter(g0) = 1.71
    c: Diameter(g1) = 1.71
    c: Diameter(g2) = 1.71
    c: Diameter(g3) = 1.71
    c: Diameter(g4) = 1.71
    c: Diameter(g5) = 1.71
    c: Diameter(g6) = 1.71
    c: Diameter(g7) = 1.71
    c: Diameter(g8) = 1.71
    c: Diameter(g9) = 1.71
    c: Vertical(g9,g1)
    c: Vertical(g1,g3)
    c: Vertical(g4,g3)
    c: Vertical(g7,g4)
    c: Vertical(g8,g6)
    c: Vertical(g6,g5)
    c: Vertical(g5,g2)
    c: Vertical(g0,g2)
    c: Horizontal(g2,g1)
    c: Horizontal(g3,g5)
    c: Horizontal(g4,g6)
    c: Horizontal(g7,g8)
    c: DistanceX(g7,g-1) = 44.8
    c: DistanceX(g-1,g8) = 44.8
    c: DistanceY(g-1,g7) = 30
    c: DistanceY(g-1,g4) = 94
    c: DistanceY(g-1,g3) = 112
    c: DistanceY(g-1,g1) = 135
    c: DistanceY(g-1,g9) = 157
    c: Diameter(g11) = 1.71
    c: Diameter(g10) = 1.71
    c: Horizontal(g9,g0)
    c: Vertical(g0,g11)
    c: Horizontal(g10,g11)
    c: Vertical(g10,g9)
    c: DistanceY(g-1,g10) = 230
FEATURE [PartDesign::Hole] Hole002  label="Plate Connection Holes"
  BaseFeature = -> Mirrored
  CustomThreadClearance = 0
  Depth = 25
  DepthType = 0
  Diameter = 1.71
  DrillForDepth = false
  DrillPoint = 1
  DrillPointAngle = 118
  HoleCutCountersinkAngle = 90
  HoleCutCustomValues = false
  HoleCutDepth = 0
  HoleCutDiameter = 3.5
  HoleCutType = 2
  ModelThread = false
  Placement = pos=(0,0,0) rot=(1,0,0;1.5708rad)
  Profile = -> Sketch017
  Suppressed = false
  Tapered = false
  TaperedAngle = 90
  ThreadClass = 0
  ThreadDepth = 25
  ThreadDepthType = 0
  ThreadDirection = 0
  ThreadFit = 0
  ThreadSize = 0
  ThreadType = 0
  Threaded = false
  UseCustomThreadClearance = false
  expr: Diameter = <<Monitor Chassis Parameters>>.GSTowerLayerJoinScrewDiameter
  expr: HoleCutDiameter = <<Monitor Chassis Parameters>>.GSM2BoltCountersinkDiameter
FEATURE [PartDesign::Body] Body  label="Backplate Body - Compute Board Variant"
  AllowCompound = false
  Group = -> [Sketch,Sketch001,Pad,Pad001,Sketch002,Pad002,Sketch003,Hole,DatumPlane,Sketch004,Pad003,Mirrored,DatumPlane007,Sketch017,Hole002]
  Origin = -> Origin001
  Placement = pos=(0.2,-1,0) rot=(0,0,1;0rad)
  Tip = -> Hole002
FEATURE [App::Part] Part  label="Tower Part"
  Group = -> [Body,Body001]
  Origin = -> Origin
